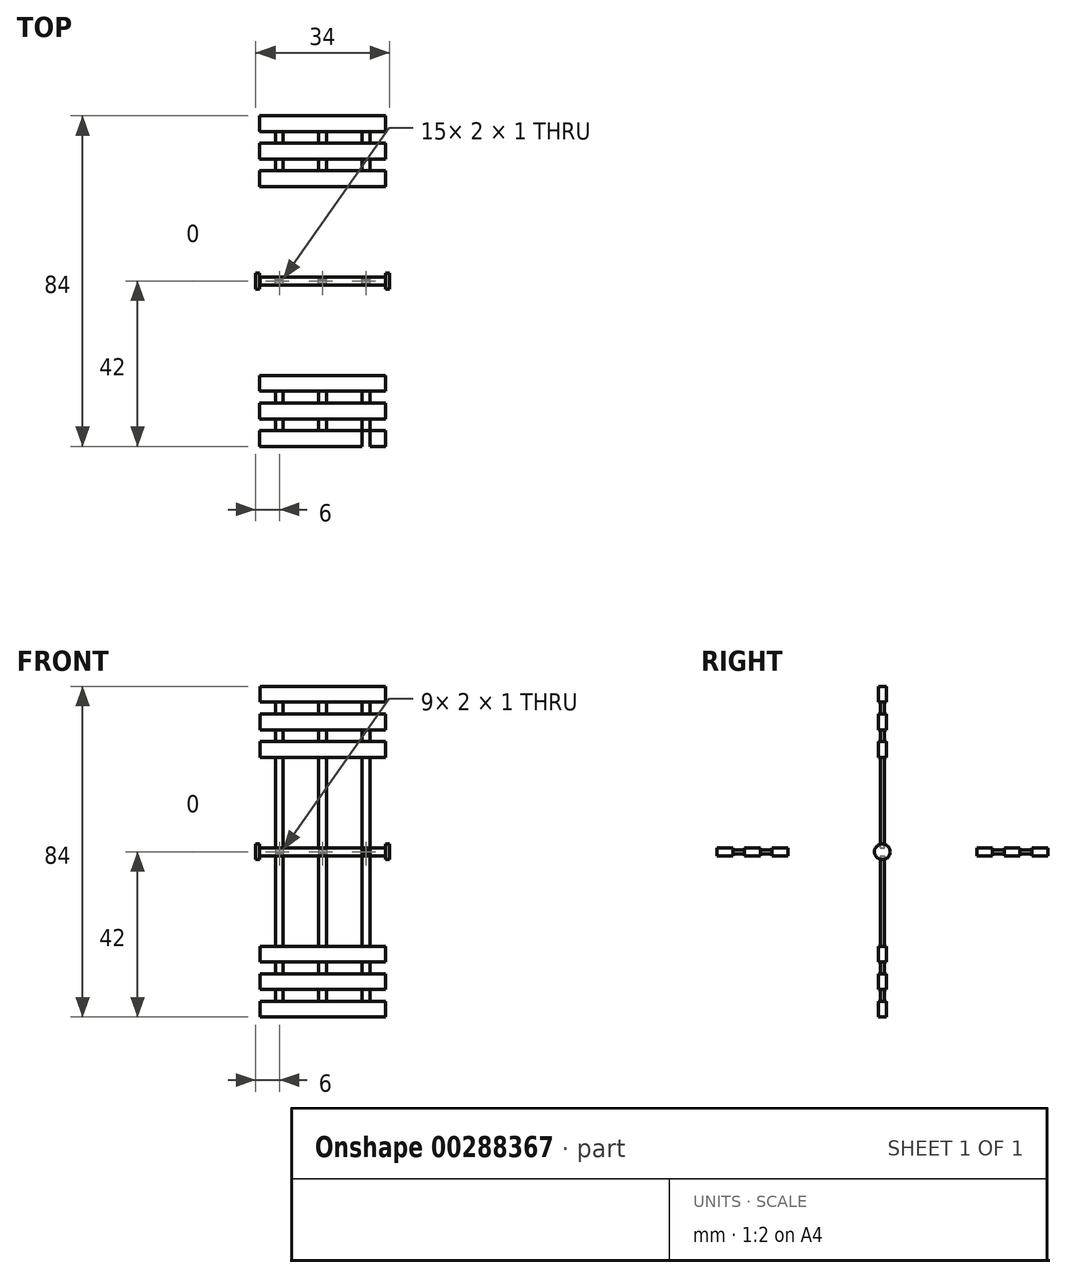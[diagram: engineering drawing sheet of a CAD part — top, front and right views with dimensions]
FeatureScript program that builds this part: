
annotation { "Feature Type Name" : "Feature", "Feature Type Description" : "" }
export const myFeature = defineFeature(function(context is Context, id is Id, definition is map)
    precondition{}
    {
        {
            var Q0;
            Q0=qCreatedBy(makeId("Top.planeOp"),FACE);
            var sketch = newSketch(context, id + "F0", { "sketchPlane" : qUnion([Q0])});
            skLineSegment(sketch, "E0.bottom", {"start": v(16, 1) * mm, "end": v(-16, 1) * mm});
            skLineSegment(sketch, "E0.top", {"start": v(16, -1) * mm, "end": v(-16, -1) * mm});
            skLineSegment(sketch, "E0.left", {"start": v(16, 1) * mm, "end": v(16, -1) * mm});
            skLineSegment(sketch, "E0.right", {"start": v(-16, 1) * mm, "end": v(-16, -1) * mm});
            skPoint(sketch, "E0.middle", {"position": v(0, 0) * mm});
            skLineSegment(sketch, "E1.bottom", {"start": v(16, 2) * mm, "end": v(17, 2) * mm});
            skLineSegment(sketch, "E1.right", {"start": v(17, 2) * mm, "end": v(17, -2) * mm});
            skPoint(sketch, "E1.middle", {"position": v(16.5, 0) * mm});
            skLineSegment(sketch, "E2.MirrorCS", {"start": v(-16, 1) * mm, "end": v(16, 1) * mm});
            skLineSegment(sketch, "E3.MirrorCS", {"start": v(-16, -1) * mm, "end": v(16, -1) * mm});
            skLineSegment(sketch, "E4.MirrorCS", {"start": v(-17, 2) * mm, "end": v(-17, -2) * mm});
            skLineSegment(sketch, "E5.MirrorCS", {"start": v(-16, 2) * mm, "end": v(-17, 2) * mm});
            skPoint(sketch, "E6.MirrorP", {"position": v(-16.5, 0) * mm});
            skLineSegment(sketch, "E7.MirrorCS", {"start": v(-16, -2) * mm, "end": v(-17, -2) * mm});
            skLineSegment(sketch, "E8.bottom", {"start": v(1, 1) * mm, "end": v(-1, 1) * mm});
            skLineSegment(sketch, "E8.top", {"start": v(1, 42) * mm, "end": v(-1, 42) * mm});
            skLineSegment(sketch, "E8.left", {"start": v(1, 1) * mm, "end": v(1, 42) * mm});
            skLineSegment(sketch, "E8.right", {"start": v(-1, 1) * mm, "end": v(-1, 42) * mm});
            skPoint(sketch, "E8.middle", {"position": v(0, 21.5) * mm});
            skPoint(sketch, "E8.middle.positionSnap0", {"position": v(0, 1) * mm});
            skPoint(sketch, "E8.centerSnap0", {"position": v(0, 1) * mm});
            skLineSegment(sketch, "E9", {"start": v(1, 6.73) * mm, "end": v(11, 6.73) * mm, "construction": true});
            skLineSegment(sketch, "E10.bottom", {"start": v(12, 1) * mm, "end": v(10, 1) * mm});
            skLineSegment(sketch, "E10.top", {"start": v(12, 42) * mm, "end": v(10, 42) * mm});
            skLineSegment(sketch, "E10.left", {"start": v(12, 1) * mm, "end": v(12, 42) * mm});
            skLineSegment(sketch, "E10.right", {"start": v(10, 1) * mm, "end": v(10, 42) * mm});
            skPoint(sketch, "E10.middle", {"position": v(11, 21.5) * mm});
            skPoint(sketch, "E10.middle.positionSnap0", {"position": v(1, 21.5) * mm});
            skPoint(sketch, "E10.centerSnap0", {"position": v(1, 21.5) * mm});
            skLineSegment(sketch, "E11.MirrorCS", {"start": v(-12, 42) * mm, "end": v(-10, 42) * mm});
            skPoint(sketch, "E12.MirrorP", {"position": v(-11, 21.5) * mm});
            skLineSegment(sketch, "E13.MirrorCS", {"start": v(-12, 1) * mm, "end": v(-10, 1) * mm});
            skLineSegment(sketch, "E14.MirrorCS", {"start": v(-12, 1) * mm, "end": v(-12, 42) * mm});
            skLineSegment(sketch, "E15.MirrorCS", {"start": v(-10, 1) * mm, "end": v(-10, 42) * mm});
            skLineSegment(sketch, "E16", {"start": v(5.79, 42) * mm, "end": v(5.79, 40) * mm, "construction": true});
            skLineSegment(sketch, "E17.bottom", {"start": v(-16, 42) * mm, "end": v(16, 42) * mm});
            skLineSegment(sketch, "E17.top", {"start": v(-16, 38) * mm, "end": v(16, 38) * mm});
            skLineSegment(sketch, "E17.left", {"start": v(-16, 42) * mm, "end": v(-16, 38) * mm});
            skLineSegment(sketch, "E17.right", {"start": v(16, 42) * mm, "end": v(16, 38) * mm});
            skPoint(sketch, "E17.middle", {"position": v(0, 40) * mm});
            skLineSegment(sketch, "E18", {"start": v(16, 38) * mm, "end": v(16, 35) * mm, "construction": true});
            skLineSegment(sketch, "E19.bottom", {"start": v(16, 35) * mm, "end": v(-16, 35) * mm});
            skLineSegment(sketch, "E19.top", {"start": v(16, 31) * mm, "end": v(-16, 31) * mm});
            skLineSegment(sketch, "E19.left", {"start": v(16, 35) * mm, "end": v(16, 31) * mm});
            skLineSegment(sketch, "E19.right", {"start": v(-16, 35) * mm, "end": v(-16, 31) * mm});
            skLineSegment(sketch, "E20", {"start": v(16, 31) * mm, "end": v(16, 28) * mm, "construction": true});
            skLineSegment(sketch, "E21.bottom", {"start": v(16, 28) * mm, "end": v(-16, 28) * mm});
            skLineSegment(sketch, "E21.top", {"start": v(16, 24) * mm, "end": v(-16, 24) * mm});
            skLineSegment(sketch, "E21.left", {"start": v(16, 28) * mm, "end": v(16, 24) * mm});
            skLineSegment(sketch, "E21.right", {"start": v(-16, 28) * mm, "end": v(-16, 24) * mm});
            skLineSegment(sketch, "E22.MirrorCS", {"start": v(16, -2) * mm, "end": v(17, -2) * mm});
            skLineSegment(sketch, "E23.MirrorCS", {"start": v(12, -42) * mm, "end": v(10, -42) * mm});
            skLineSegment(sketch, "E24.MirrorCS", {"start": v(-16, -2) * mm, "end": v(-16, 2) * mm});
            skLineSegment(sketch, "E25.MirrorCS", {"start": v(16, -2) * mm, "end": v(16, 2) * mm});
            skPoint(sketch, "E26.MirrorP", {"position": v(0, -1) * mm});
            skLineSegment(sketch, "E27.MirrorCS", {"start": v(5.79, -42) * mm, "end": v(5.79, -40) * mm, "construction": true});
            skPoint(sketch, "E28.MirrorP", {"position": v(1, -21.5) * mm});
            skLineSegment(sketch, "E29.MirrorCS", {"start": v(16, -35) * mm, "end": v(-16, -35) * mm});
            skPoint(sketch, "E30.MirrorP", {"position": v(0, -21.5) * mm});
            skLineSegment(sketch, "E31.MirrorCS", {"start": v(-1, -1) * mm, "end": v(-1, -42) * mm});
            skLineSegment(sketch, "E32.MirrorCS", {"start": v(16, -28) * mm, "end": v(16, -24) * mm});
            skLineSegment(sketch, "E33.MirrorCS", {"start": v(16, -38) * mm, "end": v(16, -35) * mm, "construction": true});
            skLineSegment(sketch, "E34.MirrorCS", {"start": v(1, -1) * mm, "end": v(1, -42) * mm});
            skLineSegment(sketch, "E35.MirrorCS", {"start": v(-12, -42) * mm, "end": v(-10, -42) * mm});
            skLineSegment(sketch, "E36.MirrorCS", {"start": v(-16, -28) * mm, "end": v(-16, -24) * mm});
            skLineSegment(sketch, "E37.MirrorCS", {"start": v(-12, -1) * mm, "end": v(-12, -42) * mm});
            skLineSegment(sketch, "E38.MirrorCS", {"start": v(1, -6.73) * mm, "end": v(11, -6.73) * mm, "construction": true});
            skLineSegment(sketch, "E39.MirrorCS", {"start": v(16, -42) * mm, "end": v(16, -38) * mm});
            skLineSegment(sketch, "E40.MirrorCS", {"start": v(16, -24) * mm, "end": v(-16, -24) * mm});
            skLineSegment(sketch, "E41.MirrorCS", {"start": v(16, -31) * mm, "end": v(-16, -31) * mm});
            skLineSegment(sketch, "E42.MirrorCS", {"start": v(1, -42) * mm, "end": v(-1, -42) * mm});
            skPoint(sketch, "E43.MirrorP", {"position": v(0, -40) * mm});
            skLineSegment(sketch, "E44.MirrorCS", {"start": v(-16, -42) * mm, "end": v(16, -42) * mm});
            skLineSegment(sketch, "E45.MirrorCS", {"start": v(16, -35) * mm, "end": v(16, -31) * mm});
            skLineSegment(sketch, "E46.MirrorCS", {"start": v(-10, -1) * mm, "end": v(-10, -42) * mm});
            skPoint(sketch, "E47.MirrorP", {"position": v(11, -21.5) * mm});
            skLineSegment(sketch, "E48.MirrorCS", {"start": v(-16, -35) * mm, "end": v(-16, -31) * mm});
            skLineSegment(sketch, "E49.MirrorCS", {"start": v(-16, -38) * mm, "end": v(16, -38) * mm});
            skLineSegment(sketch, "E50.MirrorCS", {"start": v(12, -1) * mm, "end": v(12, -42) * mm});
            skLineSegment(sketch, "E51.MirrorCS", {"start": v(16, -31) * mm, "end": v(16, -28) * mm, "construction": true});
            skLineSegment(sketch, "E52.MirrorCS", {"start": v(-16, -42) * mm, "end": v(-16, -38) * mm});
            skLineSegment(sketch, "E53.MirrorCS", {"start": v(16, -28) * mm, "end": v(-16, -28) * mm});
            skLineSegment(sketch, "E54.MirrorCS", {"start": v(10, -1) * mm, "end": v(10, -42) * mm});
            skPoint(sketch, "E55.MirrorP", {"position": v(-11, -21.5) * mm});
            skLineSegment(sketch, "E56", {"start": v(-17, 0) * mm, "end": v(17, 0) * mm});
            skSolve(sketch);
        }
        {
            var Q0;
            {var subQ4=sQuery(id+"F0.wireOp",EDGE,"E7.MirrorCS");Q0=makeQuery(id+"F0.imprint","IMPRINT",FACE,{"disambiguationData":[TD([[makeQuery(id+"F0.imprint","IMPRINT",EDGE,{"derivedFrom":subQ4}),-1.0]])]});}
            var Q1;
            {var subQ0=sQuery(id+"F0.wireOp",EDGE,"E3.MirrorCS");var subQ5=sQuery(id+"F0.wireOp",EDGE,"E24.MirrorCS");var subQ6=makeQuery(id+"F0.imprint","INTERSECT",VERTEX,{"derivedFrom":[subQ0,subQ5]});Q1=makeQuery(id+"F0.imprint","IMPRINT",FACE,{"disambiguationData":[TD([[makeQuery(id+"F0.imprint","IMPRINT",EDGE,{"disambiguationData":[TD([[subQ6,-1.0]])],"derivedFrom":subQ0}),1.0]])]});}
            var Q2;
            {var subQ4=sQuery(id+"F0.wireOp",EDGE,"E22.MirrorCS");Q2=makeQuery(id+"F0.imprint","IMPRINT",FACE,{"disambiguationData":[TD([[makeQuery(id+"F0.imprint","IMPRINT",EDGE,{"derivedFrom":subQ4}),1.0]])]});}
            var Q3;
            Q3=sQuery(id+"F0.wireOp",EDGE,"E56");
            revolve(context, id + "F1", {"entities" : qUnion([Q0, Q1, Q2]), "axis" : qUnion([Q3]), "revolveType" : RevolveType.FULL});
        }
        {
            var Q0;
            {var subQ0=sQuery(id+"F0.wireOp",EDGE,"E37.MirrorCS");var subQ1=sQuery(id+"F0.wireOp",EDGE,"E3.MirrorCS");var subQ2=makeQuery(id+"F0.imprint","INTERSECT",VERTEX,{"derivedFrom":[subQ1,subQ0]});Q0=makeQuery(id+"F0.imprint","IMPRINT",FACE,{"disambiguationData":[TD([[makeQuery(id+"F0.imprint","IMPRINT",EDGE,{"disambiguationData":[TD([[subQ2,-1.0]])],"derivedFrom":subQ1}),-1.0]])]});}
            var Q1;
            {var subQ0=sQuery(id+"F0.wireOp",EDGE,"E31.MirrorCS");var subQ1=sQuery(id+"F0.wireOp",EDGE,"E3.MirrorCS");var subQ2=makeQuery(id+"F0.imprint","INTERSECT",VERTEX,{"derivedFrom":[subQ1,subQ0]});Q1=makeQuery(id+"F0.imprint","IMPRINT",FACE,{"disambiguationData":[TD([[makeQuery(id+"F0.imprint","IMPRINT",EDGE,{"disambiguationData":[TD([[subQ2,-1.0]])],"derivedFrom":subQ1}),-1.0]])]});}
            var Q2;
            {var subQ0=sQuery(id+"F0.wireOp",EDGE,"E50.MirrorCS");var subQ1=sQuery(id+"F0.wireOp",EDGE,"E3.MirrorCS");var subQ2=makeQuery(id+"F0.imprint","INTERSECT",VERTEX,{"derivedFrom":[subQ1,subQ0]});Q2=makeQuery(id+"F0.imprint","IMPRINT",FACE,{"disambiguationData":[TD([[makeQuery(id+"F0.imprint","IMPRINT",EDGE,{"disambiguationData":[TD([[subQ2,1.0]])],"derivedFrom":subQ1}),-1.0]])]});}
            var Q3;
            {var subQ0=sQuery(id+"F0.wireOp",EDGE,"E53.MirrorCS");var subQ1=sQuery(id+"F0.wireOp",EDGE,"E31.MirrorCS");var subQ2=makeQuery(id+"F0.imprint","INTERSECT",VERTEX,{"derivedFrom":[subQ1,subQ0]});Q3=makeQuery(id+"F0.imprint","IMPRINT",FACE,{"disambiguationData":[TD([[makeQuery(id+"F0.imprint","IMPRINT",EDGE,{"disambiguationData":[TD([[subQ2,-1.0]])],"derivedFrom":subQ1}),1.0]])]});}
            var Q4;
            {var subQ0=sQuery(id+"F0.wireOp",EDGE,"E53.MirrorCS");var subQ1=sQuery(id+"F0.wireOp",EDGE,"E37.MirrorCS");var subQ2=makeQuery(id+"F0.imprint","INTERSECT",VERTEX,{"derivedFrom":[subQ1,subQ0]});Q4=makeQuery(id+"F0.imprint","IMPRINT",FACE,{"disambiguationData":[TD([[makeQuery(id+"F0.imprint","IMPRINT",EDGE,{"disambiguationData":[TD([[subQ2,-1.0]])],"derivedFrom":subQ1}),1.0]])]});}
            var Q5;
            {var subQ0=sQuery(id+"F0.wireOp",EDGE,"E37.MirrorCS");var subQ1=sQuery(id+"F0.wireOp",EDGE,"E29.MirrorCS");var subQ2=makeQuery(id+"F0.imprint","INTERSECT",VERTEX,{"derivedFrom":[subQ1,subQ0]});Q5=makeQuery(id+"F0.imprint","IMPRINT",FACE,{"disambiguationData":[TD([[makeQuery(id+"F0.imprint","IMPRINT",EDGE,{"disambiguationData":[TD([[subQ2,1.0]])],"derivedFrom":subQ1}),1.0]])]});}
            var Q6;
            {var subQ0=sQuery(id+"F0.wireOp",EDGE,"E34.MirrorCS");var subQ1=sQuery(id+"F0.wireOp",EDGE,"E29.MirrorCS");var subQ2=makeQuery(id+"F0.imprint","INTERSECT",VERTEX,{"derivedFrom":[subQ1,subQ0]});Q6=makeQuery(id+"F0.imprint","IMPRINT",FACE,{"disambiguationData":[TD([[makeQuery(id+"F0.imprint","IMPRINT",EDGE,{"disambiguationData":[TD([[subQ2,-1.0]])],"derivedFrom":subQ1}),1.0]])]});}
            var Q7;
            {var subQ0=sQuery(id+"F0.wireOp",EDGE,"E50.MirrorCS");var subQ1=sQuery(id+"F0.wireOp",EDGE,"E41.MirrorCS");var subQ2=makeQuery(id+"F0.imprint","INTERSECT",VERTEX,{"derivedFrom":[subQ1,subQ0]});Q7=makeQuery(id+"F0.imprint","IMPRINT",FACE,{"disambiguationData":[TD([[makeQuery(id+"F0.imprint","IMPRINT",EDGE,{"disambiguationData":[TD([[subQ2,-1.0]])],"derivedFrom":subQ1}),-1.0]])]});}
            var Q8;
            {var subQ0=sQuery(id+"F0.wireOp",EDGE,"E50.MirrorCS");var subQ1=sQuery(id+"F0.wireOp",EDGE,"E29.MirrorCS");var subQ2=makeQuery(id+"F0.imprint","INTERSECT",VERTEX,{"derivedFrom":[subQ1,subQ0]});Q8=makeQuery(id+"F0.imprint","IMPRINT",FACE,{"disambiguationData":[TD([[makeQuery(id+"F0.imprint","IMPRINT",EDGE,{"disambiguationData":[TD([[subQ2,-1.0]])],"derivedFrom":subQ1}),1.0]])]});}
            var Q9;
            {var subQ0=sQuery(id+"F0.wireOp",EDGE,"E8.bottom");Q9=makeQuery(id+"F0.imprint","IMPRINT",FACE,{"disambiguationData":[TD([[makeQuery(id+"F0.imprint","IMPRINT",EDGE,{"derivedFrom":subQ0}),-1.0]])]});}
            var Q10;
            {var subQ0=sQuery(id+"F0.wireOp",EDGE,"E13.MirrorCS");Q10=makeQuery(id+"F0.imprint","IMPRINT",FACE,{"disambiguationData":[TD([[makeQuery(id+"F0.imprint","IMPRINT",EDGE,{"derivedFrom":subQ0}),1.0]])]});}
            var Q11;
            {var subQ0=sQuery(id+"F0.wireOp",EDGE,"E10.bottom");Q11=makeQuery(id+"F0.imprint","IMPRINT",FACE,{"disambiguationData":[TD([[makeQuery(id+"F0.imprint","IMPRINT",EDGE,{"derivedFrom":subQ0}),-1.0]])]});}
            var Q12;
            {var subQ0=sQuery(id+"F0.wireOp",EDGE,"E21.bottom");var subQ1=sQuery(id+"F0.wireOp",EDGE,"E14.MirrorCS");var subQ2=makeQuery(id+"F0.imprint","INTERSECT",VERTEX,{"derivedFrom":[subQ1,subQ0]});Q12=makeQuery(id+"F0.imprint","IMPRINT",FACE,{"disambiguationData":[TD([[makeQuery(id+"F0.imprint","IMPRINT",EDGE,{"disambiguationData":[TD([[subQ2,-1.0]])],"derivedFrom":subQ1}),-1.0]])]});}
            var Q13;
            {var subQ0=sQuery(id+"F0.wireOp",EDGE,"E21.bottom");var subQ1=sQuery(id+"F0.wireOp",EDGE,"E8.left");var subQ2=makeQuery(id+"F0.imprint","INTERSECT",VERTEX,{"derivedFrom":[subQ1,subQ0]});Q13=makeQuery(id+"F0.imprint","IMPRINT",FACE,{"disambiguationData":[TD([[makeQuery(id+"F0.imprint","IMPRINT",EDGE,{"disambiguationData":[TD([[subQ2,-1.0]])],"derivedFrom":subQ1}),1.0]])]});}
            var Q14;
            {var subQ0=sQuery(id+"F0.wireOp",EDGE,"E21.bottom");var subQ1=sQuery(id+"F0.wireOp",EDGE,"E10.left");var subQ2=makeQuery(id+"F0.imprint","INTERSECT",VERTEX,{"derivedFrom":[subQ1,subQ0]});Q14=makeQuery(id+"F0.imprint","IMPRINT",FACE,{"disambiguationData":[TD([[makeQuery(id+"F0.imprint","IMPRINT",EDGE,{"disambiguationData":[TD([[subQ2,-1.0]])],"derivedFrom":subQ1}),1.0]])]});}
            var Q15;
            {var subQ0=sQuery(id+"F0.wireOp",EDGE,"E19.bottom");var subQ1=sQuery(id+"F0.wireOp",EDGE,"E10.left");var subQ2=makeQuery(id+"F0.imprint","INTERSECT",VERTEX,{"derivedFrom":[subQ1,subQ0]});Q15=makeQuery(id+"F0.imprint","IMPRINT",FACE,{"disambiguationData":[TD([[makeQuery(id+"F0.imprint","IMPRINT",EDGE,{"disambiguationData":[TD([[subQ2,-1.0]])],"derivedFrom":subQ1}),1.0]])]});}
            var Q16;
            {var subQ0=sQuery(id+"F0.wireOp",EDGE,"E19.bottom");var subQ1=sQuery(id+"F0.wireOp",EDGE,"E8.left");var subQ2=makeQuery(id+"F0.imprint","INTERSECT",VERTEX,{"derivedFrom":[subQ1,subQ0]});Q16=makeQuery(id+"F0.imprint","IMPRINT",FACE,{"disambiguationData":[TD([[makeQuery(id+"F0.imprint","IMPRINT",EDGE,{"disambiguationData":[TD([[subQ2,-1.0]])],"derivedFrom":subQ1}),1.0]])]});}
            var Q17;
            {var subQ0=sQuery(id+"F0.wireOp",EDGE,"E19.bottom");var subQ1=sQuery(id+"F0.wireOp",EDGE,"E14.MirrorCS");var subQ2=makeQuery(id+"F0.imprint","INTERSECT",VERTEX,{"derivedFrom":[subQ1,subQ0]});Q17=makeQuery(id+"F0.imprint","IMPRINT",FACE,{"disambiguationData":[TD([[makeQuery(id+"F0.imprint","IMPRINT",EDGE,{"disambiguationData":[TD([[subQ2,-1.0]])],"derivedFrom":subQ1}),-1.0]])]});}
            extrude(context, id + "F2", {"entities" : qUnion([Q0, Q1, Q2, Q3, Q4, Q5, Q6, Q7, Q8, Q9, Q10, Q11, Q12, Q13, Q14, Q15, Q16, Q17]), "operationType" : NewBodyOperationType.ADD, "endBound" : BoundingType.SYMMETRIC, "depth" : 1 * mm});
        }
        {
            var Q0;
            {var subQ0=sQuery(id+"F0.wireOp",EDGE,"E44.MirrorCS");var subQ1=sQuery(id+"F0.wireOp",EDGE,"E31.MirrorCS");var subQ2=makeQuery(id+"F0.imprint","INTERSECT",VERTEX,{"derivedFrom":[subQ1,subQ0]});Q0=makeQuery(id+"F0.imprint","IMPRINT",FACE,{"disambiguationData":[TD([[makeQuery(id+"F0.imprint","IMPRINT",EDGE,{"disambiguationData":[TD([[subQ2,1.0]])],"derivedFrom":subQ1}),-1.0]])]});}
            var Q1;
            {var subQ0=sQuery(id+"F0.wireOp",EDGE,"E44.MirrorCS");var subQ1=sQuery(id+"F0.wireOp",EDGE,"E34.MirrorCS");var subQ2=makeQuery(id+"F0.imprint","INTERSECT",VERTEX,{"derivedFrom":[subQ1,subQ0]});Q1=makeQuery(id+"F0.imprint","IMPRINT",FACE,{"disambiguationData":[TD([[makeQuery(id+"F0.imprint","IMPRINT",EDGE,{"disambiguationData":[TD([[subQ2,1.0]])],"derivedFrom":subQ1}),1.0]])]});}
            var Q2;
            {var subQ0=sQuery(id+"F0.wireOp",EDGE,"E44.MirrorCS");var subQ1=sQuery(id+"F0.wireOp",EDGE,"E37.MirrorCS");var subQ2=makeQuery(id+"F0.imprint","INTERSECT",VERTEX,{"derivedFrom":[subQ1,subQ0]});Q2=makeQuery(id+"F0.imprint","IMPRINT",FACE,{"disambiguationData":[TD([[makeQuery(id+"F0.imprint","IMPRINT",EDGE,{"disambiguationData":[TD([[subQ2,1.0]])],"derivedFrom":subQ1}),1.0]])]});}
            var Q3;
            {var subQ0=sQuery(id+"F0.wireOp",EDGE,"E50.MirrorCS");var subQ1=sQuery(id+"F0.wireOp",EDGE,"E44.MirrorCS");var subQ2=makeQuery(id+"F0.imprint","INTERSECT",VERTEX,{"derivedFrom":[subQ1,subQ0]});Q3=makeQuery(id+"F0.imprint","IMPRINT",FACE,{"disambiguationData":[TD([[makeQuery(id+"F0.imprint","IMPRINT",EDGE,{"disambiguationData":[TD([[subQ2,1.0]])],"derivedFrom":subQ1}),1.0]])]});}
            var Q4;
            {var subQ5=sQuery(id+"F0.wireOp",EDGE,"E52.MirrorCS");Q4=makeQuery(id+"F0.imprint","IMPRINT",FACE,{"disambiguationData":[TD([[makeQuery(id+"F0.imprint","IMPRINT",EDGE,{"derivedFrom":subQ5}),-1.0]])]});}
            var Q5;
            {var subQ0=sQuery(id+"F0.wireOp",EDGE,"E39.MirrorCS");Q5=makeQuery(id+"F0.imprint","IMPRINT",FACE,{"disambiguationData":[TD([[makeQuery(id+"F0.imprint","IMPRINT",EDGE,{"derivedFrom":subQ0}),1.0]])]});}
            var Q6;
            {var subQ0=sQuery(id+"F0.wireOp",EDGE,"E44.MirrorCS");var subQ1=sQuery(id+"F0.wireOp",EDGE,"E31.MirrorCS");var subQ2=makeQuery(id+"F0.imprint","INTERSECT",VERTEX,{"derivedFrom":[subQ1,subQ0]});Q6=makeQuery(id+"F0.imprint","IMPRINT",FACE,{"disambiguationData":[TD([[makeQuery(id+"F0.imprint","IMPRINT",EDGE,{"disambiguationData":[TD([[subQ2,1.0]])],"derivedFrom":subQ1}),1.0]])]});}
            var Q7;
            {var subQ0=sQuery(id+"F0.wireOp",EDGE,"E45.MirrorCS");Q7=makeQuery(id+"F0.imprint","IMPRINT",FACE,{"disambiguationData":[TD([[makeQuery(id+"F0.imprint","IMPRINT",EDGE,{"derivedFrom":subQ0}),1.0]])]});}
            var Q8;
            {var subQ0=sQuery(id+"F0.wireOp",EDGE,"E50.MirrorCS");var subQ1=sQuery(id+"F0.wireOp",EDGE,"E29.MirrorCS");var subQ2=makeQuery(id+"F0.imprint","INTERSECT",VERTEX,{"derivedFrom":[subQ1,subQ0]});Q8=makeQuery(id+"F0.imprint","IMPRINT",FACE,{"disambiguationData":[TD([[makeQuery(id+"F0.imprint","IMPRINT",EDGE,{"disambiguationData":[TD([[subQ2,-1.0]])],"derivedFrom":subQ1}),-1.0]])]});}
            var Q9;
            {var subQ0=sQuery(id+"F0.wireOp",EDGE,"E54.MirrorCS");var subQ1=sQuery(id+"F0.wireOp",EDGE,"E29.MirrorCS");var subQ2=makeQuery(id+"F0.imprint","INTERSECT",VERTEX,{"derivedFrom":[subQ1,subQ0]});Q9=makeQuery(id+"F0.imprint","IMPRINT",FACE,{"disambiguationData":[TD([[makeQuery(id+"F0.imprint","IMPRINT",EDGE,{"disambiguationData":[TD([[subQ2,-1.0]])],"derivedFrom":subQ1}),-1.0]])]});}
            var Q10;
            {var subQ0=sQuery(id+"F0.wireOp",EDGE,"E34.MirrorCS");var subQ1=sQuery(id+"F0.wireOp",EDGE,"E29.MirrorCS");var subQ2=makeQuery(id+"F0.imprint","INTERSECT",VERTEX,{"derivedFrom":[subQ1,subQ0]});Q10=makeQuery(id+"F0.imprint","IMPRINT",FACE,{"disambiguationData":[TD([[makeQuery(id+"F0.imprint","IMPRINT",EDGE,{"disambiguationData":[TD([[subQ2,-1.0]])],"derivedFrom":subQ1}),-1.0]])]});}
            var Q11;
            {var subQ0=sQuery(id+"F0.wireOp",EDGE,"E31.MirrorCS");var subQ1=sQuery(id+"F0.wireOp",EDGE,"E29.MirrorCS");var subQ2=makeQuery(id+"F0.imprint","INTERSECT",VERTEX,{"derivedFrom":[subQ1,subQ0]});Q11=makeQuery(id+"F0.imprint","IMPRINT",FACE,{"disambiguationData":[TD([[makeQuery(id+"F0.imprint","IMPRINT",EDGE,{"disambiguationData":[TD([[subQ2,-1.0]])],"derivedFrom":subQ1}),-1.0]])]});}
            var Q12;
            {var subQ0=sQuery(id+"F0.wireOp",EDGE,"E37.MirrorCS");var subQ1=sQuery(id+"F0.wireOp",EDGE,"E29.MirrorCS");var subQ2=makeQuery(id+"F0.imprint","INTERSECT",VERTEX,{"derivedFrom":[subQ1,subQ0]});Q12=makeQuery(id+"F0.imprint","IMPRINT",FACE,{"disambiguationData":[TD([[makeQuery(id+"F0.imprint","IMPRINT",EDGE,{"disambiguationData":[TD([[subQ2,1.0]])],"derivedFrom":subQ1}),-1.0]])]});}
            var Q13;
            {var subQ0=sQuery(id+"F0.wireOp",EDGE,"E48.MirrorCS");Q13=makeQuery(id+"F0.imprint","IMPRINT",FACE,{"disambiguationData":[TD([[makeQuery(id+"F0.imprint","IMPRINT",EDGE,{"derivedFrom":subQ0}),-1.0]])]});}
            var Q14;
            {var subQ0=sQuery(id+"F0.wireOp",EDGE,"E36.MirrorCS");Q14=makeQuery(id+"F0.imprint","IMPRINT",FACE,{"disambiguationData":[TD([[makeQuery(id+"F0.imprint","IMPRINT",EDGE,{"derivedFrom":subQ0}),-1.0]])]});}
            var Q15;
            {var subQ0=sQuery(id+"F0.wireOp",EDGE,"E40.MirrorCS");var subQ1=sQuery(id+"F0.wireOp",EDGE,"E37.MirrorCS");var subQ2=makeQuery(id+"F0.imprint","INTERSECT",VERTEX,{"derivedFrom":[subQ1,subQ0]});Q15=makeQuery(id+"F0.imprint","IMPRINT",FACE,{"disambiguationData":[TD([[makeQuery(id+"F0.imprint","IMPRINT",EDGE,{"disambiguationData":[TD([[subQ2,-1.0]])],"derivedFrom":subQ1}),1.0]])]});}
            var Q16;
            {var subQ0=sQuery(id+"F0.wireOp",EDGE,"E40.MirrorCS");var subQ1=sQuery(id+"F0.wireOp",EDGE,"E31.MirrorCS");var subQ2=makeQuery(id+"F0.imprint","INTERSECT",VERTEX,{"derivedFrom":[subQ1,subQ0]});Q16=makeQuery(id+"F0.imprint","IMPRINT",FACE,{"disambiguationData":[TD([[makeQuery(id+"F0.imprint","IMPRINT",EDGE,{"disambiguationData":[TD([[subQ2,-1.0]])],"derivedFrom":subQ1}),-1.0]])]});}
            var Q17;
            {var subQ0=sQuery(id+"F0.wireOp",EDGE,"E40.MirrorCS");var subQ1=sQuery(id+"F0.wireOp",EDGE,"E31.MirrorCS");var subQ2=makeQuery(id+"F0.imprint","INTERSECT",VERTEX,{"derivedFrom":[subQ1,subQ0]});Q17=makeQuery(id+"F0.imprint","IMPRINT",FACE,{"disambiguationData":[TD([[makeQuery(id+"F0.imprint","IMPRINT",EDGE,{"disambiguationData":[TD([[subQ2,-1.0]])],"derivedFrom":subQ1}),1.0]])]});}
            var Q18;
            {var subQ0=sQuery(id+"F0.wireOp",EDGE,"E40.MirrorCS");var subQ1=sQuery(id+"F0.wireOp",EDGE,"E34.MirrorCS");var subQ2=makeQuery(id+"F0.imprint","INTERSECT",VERTEX,{"derivedFrom":[subQ1,subQ0]});Q18=makeQuery(id+"F0.imprint","IMPRINT",FACE,{"disambiguationData":[TD([[makeQuery(id+"F0.imprint","IMPRINT",EDGE,{"disambiguationData":[TD([[subQ2,-1.0]])],"derivedFrom":subQ1}),1.0]])]});}
            var Q19;
            {var subQ0=sQuery(id+"F0.wireOp",EDGE,"E50.MirrorCS");var subQ1=sQuery(id+"F0.wireOp",EDGE,"E40.MirrorCS");var subQ2=makeQuery(id+"F0.imprint","INTERSECT",VERTEX,{"derivedFrom":[subQ1,subQ0]});Q19=makeQuery(id+"F0.imprint","IMPRINT",FACE,{"disambiguationData":[TD([[makeQuery(id+"F0.imprint","IMPRINT",EDGE,{"disambiguationData":[TD([[subQ2,-1.0]])],"derivedFrom":subQ1}),1.0]])]});}
            var Q20;
            {var subQ0=sQuery(id+"F0.wireOp",EDGE,"E32.MirrorCS");Q20=makeQuery(id+"F0.imprint","IMPRINT",FACE,{"disambiguationData":[TD([[makeQuery(id+"F0.imprint","IMPRINT",EDGE,{"derivedFrom":subQ0}),1.0]])]});}
            var Q21;
            {var subQ5=sQuery(id+"F0.wireOp",EDGE,"E21.left");Q21=makeQuery(id+"F0.imprint","IMPRINT",FACE,{"disambiguationData":[TD([[makeQuery(id+"F0.imprint","IMPRINT",EDGE,{"derivedFrom":subQ5}),-1.0]])]});}
            var Q22;
            {var subQ0=sQuery(id+"F0.wireOp",EDGE,"E21.top");var subQ1=sQuery(id+"F0.wireOp",EDGE,"E10.left");var subQ2=makeQuery(id+"F0.imprint","INTERSECT",VERTEX,{"derivedFrom":[subQ1,subQ0]});Q22=makeQuery(id+"F0.imprint","IMPRINT",FACE,{"disambiguationData":[TD([[makeQuery(id+"F0.imprint","IMPRINT",EDGE,{"disambiguationData":[TD([[subQ2,-1.0]])],"derivedFrom":subQ1}),1.0]])]});}
            var Q23;
            {var subQ0=sQuery(id+"F0.wireOp",EDGE,"E21.top");var subQ1=sQuery(id+"F0.wireOp",EDGE,"E8.left");var subQ2=makeQuery(id+"F0.imprint","INTERSECT",VERTEX,{"derivedFrom":[subQ1,subQ0]});Q23=makeQuery(id+"F0.imprint","IMPRINT",FACE,{"disambiguationData":[TD([[makeQuery(id+"F0.imprint","IMPRINT",EDGE,{"disambiguationData":[TD([[subQ2,-1.0]])],"derivedFrom":subQ1}),-1.0]])]});}
            var Q24;
            {var subQ0=sQuery(id+"F0.wireOp",EDGE,"E21.top");var subQ1=sQuery(id+"F0.wireOp",EDGE,"E8.left");var subQ2=makeQuery(id+"F0.imprint","INTERSECT",VERTEX,{"derivedFrom":[subQ1,subQ0]});Q24=makeQuery(id+"F0.imprint","IMPRINT",FACE,{"disambiguationData":[TD([[makeQuery(id+"F0.imprint","IMPRINT",EDGE,{"disambiguationData":[TD([[subQ2,-1.0]])],"derivedFrom":subQ1}),1.0]])]});}
            var Q25;
            {var subQ0=sQuery(id+"F0.wireOp",EDGE,"E21.top");var subQ1=sQuery(id+"F0.wireOp",EDGE,"E8.right");var subQ2=makeQuery(id+"F0.imprint","INTERSECT",VERTEX,{"derivedFrom":[subQ1,subQ0]});Q25=makeQuery(id+"F0.imprint","IMPRINT",FACE,{"disambiguationData":[TD([[makeQuery(id+"F0.imprint","IMPRINT",EDGE,{"disambiguationData":[TD([[subQ2,-1.0]])],"derivedFrom":subQ1}),1.0]])]});}
            var Q26;
            {var subQ0=sQuery(id+"F0.wireOp",EDGE,"E21.top");var subQ1=sQuery(id+"F0.wireOp",EDGE,"E14.MirrorCS");var subQ2=makeQuery(id+"F0.imprint","INTERSECT",VERTEX,{"derivedFrom":[subQ1,subQ0]});Q26=makeQuery(id+"F0.imprint","IMPRINT",FACE,{"disambiguationData":[TD([[makeQuery(id+"F0.imprint","IMPRINT",EDGE,{"disambiguationData":[TD([[subQ2,-1.0]])],"derivedFrom":subQ1}),-1.0]])]});}
            var Q27;
            {var subQ5=sQuery(id+"F0.wireOp",EDGE,"E21.right");Q27=makeQuery(id+"F0.imprint","IMPRINT",FACE,{"disambiguationData":[TD([[makeQuery(id+"F0.imprint","IMPRINT",EDGE,{"derivedFrom":subQ5}),1.0]])]});}
            var Q28;
            {var subQ5=sQuery(id+"F0.wireOp",EDGE,"E19.right");Q28=makeQuery(id+"F0.imprint","IMPRINT",FACE,{"disambiguationData":[TD([[makeQuery(id+"F0.imprint","IMPRINT",EDGE,{"derivedFrom":subQ5}),1.0]])]});}
            var Q29;
            {var subQ0=sQuery(id+"F0.wireOp",EDGE,"E19.top");var subQ1=sQuery(id+"F0.wireOp",EDGE,"E14.MirrorCS");var subQ2=makeQuery(id+"F0.imprint","INTERSECT",VERTEX,{"derivedFrom":[subQ1,subQ0]});Q29=makeQuery(id+"F0.imprint","IMPRINT",FACE,{"disambiguationData":[TD([[makeQuery(id+"F0.imprint","IMPRINT",EDGE,{"disambiguationData":[TD([[subQ2,-1.0]])],"derivedFrom":subQ1}),-1.0]])]});}
            var Q30;
            {var subQ0=sQuery(id+"F0.wireOp",EDGE,"E19.top");var subQ1=sQuery(id+"F0.wireOp",EDGE,"E8.right");var subQ2=makeQuery(id+"F0.imprint","INTERSECT",VERTEX,{"derivedFrom":[subQ1,subQ0]});Q30=makeQuery(id+"F0.imprint","IMPRINT",FACE,{"disambiguationData":[TD([[makeQuery(id+"F0.imprint","IMPRINT",EDGE,{"disambiguationData":[TD([[subQ2,-1.0]])],"derivedFrom":subQ1}),1.0]])]});}
            var Q31;
            {var subQ0=sQuery(id+"F0.wireOp",EDGE,"E19.top");var subQ1=sQuery(id+"F0.wireOp",EDGE,"E8.left");var subQ2=makeQuery(id+"F0.imprint","INTERSECT",VERTEX,{"derivedFrom":[subQ1,subQ0]});Q31=makeQuery(id+"F0.imprint","IMPRINT",FACE,{"disambiguationData":[TD([[makeQuery(id+"F0.imprint","IMPRINT",EDGE,{"disambiguationData":[TD([[subQ2,-1.0]])],"derivedFrom":subQ1}),1.0]])]});}
            var Q32;
            {var subQ0=sQuery(id+"F0.wireOp",EDGE,"E19.top");var subQ1=sQuery(id+"F0.wireOp",EDGE,"E8.left");var subQ2=makeQuery(id+"F0.imprint","INTERSECT",VERTEX,{"derivedFrom":[subQ1,subQ0]});Q32=makeQuery(id+"F0.imprint","IMPRINT",FACE,{"disambiguationData":[TD([[makeQuery(id+"F0.imprint","IMPRINT",EDGE,{"disambiguationData":[TD([[subQ2,-1.0]])],"derivedFrom":subQ1}),-1.0]])]});}
            var Q33;
            {var subQ0=sQuery(id+"F0.wireOp",EDGE,"E19.top");var subQ1=sQuery(id+"F0.wireOp",EDGE,"E10.left");var subQ2=makeQuery(id+"F0.imprint","INTERSECT",VERTEX,{"derivedFrom":[subQ1,subQ0]});Q33=makeQuery(id+"F0.imprint","IMPRINT",FACE,{"disambiguationData":[TD([[makeQuery(id+"F0.imprint","IMPRINT",EDGE,{"disambiguationData":[TD([[subQ2,-1.0]])],"derivedFrom":subQ1}),1.0]])]});}
            var Q34;
            {var subQ5=sQuery(id+"F0.wireOp",EDGE,"E19.left");Q34=makeQuery(id+"F0.imprint","IMPRINT",FACE,{"disambiguationData":[TD([[makeQuery(id+"F0.imprint","IMPRINT",EDGE,{"derivedFrom":subQ5}),-1.0]])]});}
            var Q35;
            {var subQ5=sQuery(id+"F0.wireOp",EDGE,"E17.right");Q35=makeQuery(id+"F0.imprint","IMPRINT",FACE,{"disambiguationData":[TD([[makeQuery(id+"F0.imprint","IMPRINT",EDGE,{"derivedFrom":subQ5}),-1.0]])]});}
            var Q36;
            {var subQ0=sQuery(id+"F0.wireOp",EDGE,"E17.bottom");var subQ1=sQuery(id+"F0.wireOp",EDGE,"E10.left");var subQ2=makeQuery(id+"F0.imprint","INTERSECT",VERTEX,{"derivedFrom":[subQ1,subQ0]});Q36=makeQuery(id+"F0.imprint","IMPRINT",FACE,{"disambiguationData":[TD([[makeQuery(id+"F0.imprint","IMPRINT",EDGE,{"disambiguationData":[TD([[subQ2,1.0]])],"derivedFrom":subQ1}),1.0]])]});}
            var Q37;
            {var subQ0=sQuery(id+"F0.wireOp",EDGE,"E17.bottom");var subQ1=sQuery(id+"F0.wireOp",EDGE,"E8.left");var subQ2=makeQuery(id+"F0.imprint","INTERSECT",VERTEX,{"derivedFrom":[subQ1,subQ0]});Q37=makeQuery(id+"F0.imprint","IMPRINT",FACE,{"disambiguationData":[TD([[makeQuery(id+"F0.imprint","IMPRINT",EDGE,{"disambiguationData":[TD([[subQ2,1.0]])],"derivedFrom":subQ1}),-1.0]])]});}
            var Q38;
            {var subQ0=sQuery(id+"F0.wireOp",EDGE,"E17.bottom");var subQ1=sQuery(id+"F0.wireOp",EDGE,"E8.left");var subQ2=makeQuery(id+"F0.imprint","INTERSECT",VERTEX,{"derivedFrom":[subQ1,subQ0]});Q38=makeQuery(id+"F0.imprint","IMPRINT",FACE,{"disambiguationData":[TD([[makeQuery(id+"F0.imprint","IMPRINT",EDGE,{"disambiguationData":[TD([[subQ2,1.0]])],"derivedFrom":subQ1}),1.0]])]});}
            var Q39;
            {var subQ0=sQuery(id+"F0.wireOp",EDGE,"E17.bottom");var subQ1=sQuery(id+"F0.wireOp",EDGE,"E8.right");var subQ2=makeQuery(id+"F0.imprint","INTERSECT",VERTEX,{"derivedFrom":[subQ1,subQ0]});Q39=makeQuery(id+"F0.imprint","IMPRINT",FACE,{"disambiguationData":[TD([[makeQuery(id+"F0.imprint","IMPRINT",EDGE,{"disambiguationData":[TD([[subQ2,1.0]])],"derivedFrom":subQ1}),1.0]])]});}
            var Q40;
            {var subQ0=sQuery(id+"F0.wireOp",EDGE,"E17.bottom");var subQ1=sQuery(id+"F0.wireOp",EDGE,"E14.MirrorCS");var subQ2=makeQuery(id+"F0.imprint","INTERSECT",VERTEX,{"derivedFrom":[subQ1,subQ0]});Q40=makeQuery(id+"F0.imprint","IMPRINT",FACE,{"disambiguationData":[TD([[makeQuery(id+"F0.imprint","IMPRINT",EDGE,{"disambiguationData":[TD([[subQ2,1.0]])],"derivedFrom":subQ1}),-1.0]])]});}
            var Q41;
            {var subQ5=sQuery(id+"F0.wireOp",EDGE,"E17.left");Q41=makeQuery(id+"F0.imprint","IMPRINT",FACE,{"disambiguationData":[TD([[makeQuery(id+"F0.imprint","IMPRINT",EDGE,{"derivedFrom":subQ5}),1.0]])]});}
            extrude(context, id + "F3", {"entities" : qUnion([Q0, Q1, Q2, Q3, Q4, Q5, Q6, Q7, Q8, Q9, Q10, Q11, Q12, Q13, Q14, Q15, Q16, Q17, Q18, Q19, Q20, Q21, Q22, Q23, Q24, Q25, Q26, Q27, Q28, Q29, Q30, Q31, Q32, Q33, Q34, Q35, Q36, Q37, Q38, Q39, Q40, Q41]), "endBound" : BoundingType.SYMMETRIC, "depth" : 2 * mm});
        }
        {
            var Q0;
            Q0=qCreatedBy(makeId("Front.planeOp"),FACE);
            var sketch = newSketch(context, id + "F4", { "sketchPlane" : qUnion([Q0])});
            skLineSegment(sketch, "E57", {"start": v(3.55, 0) * mm, "end": v(3.55, 1) * mm, "construction": true});
            skLineSegment(sketch, "E58.bottom", {"start": v(1, 1) * mm, "end": v(-1, 1) * mm});
            skLineSegment(sketch, "E58.top", {"start": v(1, 42) * mm, "end": v(-1, 42) * mm});
            skLineSegment(sketch, "E58.left", {"start": v(1, 1) * mm, "end": v(1, 42) * mm});
            skLineSegment(sketch, "E58.right", {"start": v(-1, 1) * mm, "end": v(-1, 42) * mm});
            skPoint(sketch, "E58.middle", {"position": v(0, 21.5) * mm});
            skLineSegment(sketch, "E59", {"start": v(1, 7.07) * mm, "end": v(11, 7.07) * mm, "construction": true});
            skLineSegment(sketch, "E60.bottom", {"start": v(10, 1) * mm, "end": v(12, 1) * mm});
            skLineSegment(sketch, "E60.top", {"start": v(10, 42) * mm, "end": v(12, 42) * mm});
            skLineSegment(sketch, "E60.left", {"start": v(10, 1) * mm, "end": v(10, 42) * mm});
            skLineSegment(sketch, "E60.right", {"start": v(12, 1) * mm, "end": v(12, 42) * mm});
            skPoint(sketch, "E60.middle", {"position": v(11, 21.5) * mm});
            skLineSegment(sketch, "E61", {"start": v(0, 0) * mm, "end": v(0, 4.7) * mm, "construction": true});
            skLineSegment(sketch, "E62.MirrorCS", {"start": v(-10, 1) * mm, "end": v(-10, 42) * mm});
            skLineSegment(sketch, "E63.MirrorCS", {"start": v(-12, 1) * mm, "end": v(-12, 42) * mm});
            skLineSegment(sketch, "E64.MirrorCS", {"start": v(-10, 42) * mm, "end": v(-12, 42) * mm});
            skLineSegment(sketch, "E65", {"start": v(-15.95, 1.1) * mm, "end": v(-15.95, 11.1) * mm, "construction": true});
            skLineSegment(sketch, "E66.bottom", {"start": v(-15.95, 42) * mm, "end": v(16.05, 42) * mm});
            skLineSegment(sketch, "E66.top", {"start": v(-15.95, 38) * mm, "end": v(16.05, 38) * mm});
            skLineSegment(sketch, "E66.left", {"start": v(-15.95, 42) * mm, "end": v(-15.95, 38) * mm});
            skLineSegment(sketch, "E66.right", {"start": v(16.05, 42) * mm, "end": v(16.05, 38) * mm});
            skLineSegment(sketch, "E67", {"start": v(14.26, 38) * mm, "end": v(14.26, 35) * mm, "construction": true});
            skLineSegment(sketch, "E68.bottom", {"start": v(-15.95, 35) * mm, "end": v(16.05, 35) * mm});
            skLineSegment(sketch, "E68.top", {"start": v(-15.95, 31) * mm, "end": v(16.05, 31) * mm});
            skLineSegment(sketch, "E68.left", {"start": v(-15.95, 35) * mm, "end": v(-15.95, 31) * mm});
            skLineSegment(sketch, "E68.right", {"start": v(16.05, 35) * mm, "end": v(16.05, 31) * mm});
            skLineSegment(sketch, "E69", {"start": v(14.26, 31) * mm, "end": v(14.26, 28) * mm, "construction": true});
            skLineSegment(sketch, "E70.bottom", {"start": v(-15.95, 28) * mm, "end": v(16.05, 28) * mm});
            skLineSegment(sketch, "E70.top", {"start": v(-15.95, 24) * mm, "end": v(16.05, 24) * mm});
            skLineSegment(sketch, "E70.left", {"start": v(-15.95, 28) * mm, "end": v(-15.95, 24) * mm});
            skLineSegment(sketch, "E70.right", {"start": v(16.05, 28) * mm, "end": v(16.05, 24) * mm});
            skLineSegment(sketch, "E71", {"start": v(-10, 1) * mm, "end": v(-12, 1) * mm});
            skLineSegment(sketch, "E72.MirrorCS", {"start": v(10, -42) * mm, "end": v(12, -42) * mm});
            skLineSegment(sketch, "E73.MirrorCS", {"start": v(-10, -42) * mm, "end": v(-12, -42) * mm});
            skLineSegment(sketch, "E74.MirrorCS", {"start": v(-10, -1) * mm, "end": v(-12, -1) * mm});
            skLineSegment(sketch, "E75.MirrorCS", {"start": v(10, -1) * mm, "end": v(12, -1) * mm});
            skLineSegment(sketch, "E76.MirrorCS", {"start": v(1, -42) * mm, "end": v(-1, -42) * mm});
            skLineSegment(sketch, "E77.MirrorCS", {"start": v(1, -1) * mm, "end": v(-1, -1) * mm});
            skLineSegment(sketch, "E78.MirrorCS", {"start": v(3.55, 0) * mm, "end": v(3.55, -1) * mm, "construction": true});
            skLineSegment(sketch, "E79.MirrorCS", {"start": v(-15.95, -28) * mm, "end": v(16.05, -28) * mm});
            skLineSegment(sketch, "E80.MirrorCS", {"start": v(-15.95, -42) * mm, "end": v(-15.95, -38) * mm});
            skLineSegment(sketch, "E81.MirrorCS", {"start": v(-15.95, -1.1) * mm, "end": v(-15.95, -11.1) * mm, "construction": true});
            skLineSegment(sketch, "E82.MirrorCS", {"start": v(10, -1) * mm, "end": v(10, -42) * mm});
            skLineSegment(sketch, "E83.MirrorCS", {"start": v(12, -1) * mm, "end": v(12, -42) * mm});
            skLineSegment(sketch, "E84.MirrorCS", {"start": v(-15.95, -35) * mm, "end": v(16.05, -35) * mm});
            skLineSegment(sketch, "E85.MirrorCS", {"start": v(16.05, -35) * mm, "end": v(16.05, -31) * mm});
            skLineSegment(sketch, "E86.MirrorCS", {"start": v(1, -1) * mm, "end": v(1, -42) * mm});
            skLineSegment(sketch, "E87.MirrorCS", {"start": v(0, 0) * mm, "end": v(0, -4.7) * mm, "construction": true});
            skLineSegment(sketch, "E88.MirrorCS", {"start": v(16.05, -28) * mm, "end": v(16.05, -24) * mm});
            skLineSegment(sketch, "E89.MirrorCS", {"start": v(-1, -1) * mm, "end": v(-1, -42) * mm});
            skLineSegment(sketch, "E90.MirrorCS", {"start": v(-10, -1) * mm, "end": v(-10, -42) * mm});
            skLineSegment(sketch, "E91.MirrorCS", {"start": v(-12, -1) * mm, "end": v(-12, -42) * mm});
            skLineSegment(sketch, "E92.MirrorCS", {"start": v(-15.95, -42) * mm, "end": v(16.05, -42) * mm});
            skLineSegment(sketch, "E93.MirrorCS", {"start": v(14.26, -31) * mm, "end": v(14.26, -28) * mm, "construction": true});
            skLineSegment(sketch, "E94.MirrorCS", {"start": v(-15.95, -31) * mm, "end": v(16.05, -31) * mm});
            skPoint(sketch, "E95.MirrorP", {"position": v(0, -21.5) * mm});
            skLineSegment(sketch, "E96.MirrorCS", {"start": v(16.05, -42) * mm, "end": v(16.05, -38) * mm});
            skLineSegment(sketch, "E97.MirrorCS", {"start": v(14.26, -38) * mm, "end": v(14.26, -35) * mm, "construction": true});
            skPoint(sketch, "E98.MirrorP", {"position": v(11, -21.5) * mm});
            skLineSegment(sketch, "E99.MirrorCS", {"start": v(1, -7.07) * mm, "end": v(11, -7.07) * mm, "construction": true});
            skLineSegment(sketch, "E100.MirrorCS", {"start": v(-15.95, -28) * mm, "end": v(-15.95, -24) * mm});
            skLineSegment(sketch, "E101.MirrorCS", {"start": v(-15.95, -35) * mm, "end": v(-15.95, -31) * mm});
            skLineSegment(sketch, "E102.MirrorCS", {"start": v(-15.95, -24) * mm, "end": v(16.05, -24) * mm});
            skLineSegment(sketch, "E103.MirrorCS", {"start": v(-15.95, -38) * mm, "end": v(16.05, -38) * mm});
            skSolve(sketch);
        }
        {
            var Q0;
            {var subQ0=sQuery(id+"F4.wireOp",EDGE,"E58.bottom");Q0=makeQuery(id+"F4.imprint","IMPRINT",FACE,{"disambiguationData":[TD([[makeQuery(id+"F4.imprint","IMPRINT",EDGE,{"derivedFrom":subQ0}),-1.0]])]});}
            var Q1;
            {var subQ0=sQuery(id+"F4.wireOp",EDGE,"E60.bottom");Q1=makeQuery(id+"F4.imprint","IMPRINT",FACE,{"disambiguationData":[TD([[makeQuery(id+"F4.imprint","IMPRINT",EDGE,{"derivedFrom":subQ0}),1.0]])]});}
            var Q2;
            {var subQ0=sQuery(id+"F4.wireOp",EDGE,"E71");Q2=makeQuery(id+"F4.imprint","IMPRINT",FACE,{"disambiguationData":[TD([[makeQuery(id+"F4.imprint","IMPRINT",EDGE,{"derivedFrom":subQ0}),-1.0]])]});}
            var Q3;
            {var subQ0=sQuery(id+"F4.wireOp",EDGE,"E74.MirrorCS");Q3=makeQuery(id+"F4.imprint","IMPRINT",FACE,{"disambiguationData":[TD([[makeQuery(id+"F4.imprint","IMPRINT",EDGE,{"derivedFrom":subQ0}),1.0]])]});}
            var Q4;
            {var subQ0=sQuery(id+"F4.wireOp",EDGE,"E75.MirrorCS");Q4=makeQuery(id+"F4.imprint","IMPRINT",FACE,{"disambiguationData":[TD([[makeQuery(id+"F4.imprint","IMPRINT",EDGE,{"derivedFrom":subQ0}),-1.0]])]});}
            var Q5;
            {var subQ0=sQuery(id+"F4.wireOp",EDGE,"E77.MirrorCS");Q5=makeQuery(id+"F4.imprint","IMPRINT",FACE,{"disambiguationData":[TD([[makeQuery(id+"F4.imprint","IMPRINT",EDGE,{"derivedFrom":subQ0}),1.0]])]});}
            var Q6;
            {var subQ0=sQuery(id+"F4.wireOp",EDGE,"E70.bottom");var subQ1=sQuery(id+"F4.wireOp",EDGE,"E60.left");var subQ2=makeQuery(id+"F4.imprint","INTERSECT",VERTEX,{"derivedFrom":[subQ1,subQ0]});Q6=makeQuery(id+"F4.imprint","IMPRINT",FACE,{"disambiguationData":[TD([[makeQuery(id+"F4.imprint","IMPRINT",EDGE,{"disambiguationData":[TD([[subQ2,-1.0]])],"derivedFrom":subQ1}),-1.0]])]});}
            var Q7;
            {var subQ0=sQuery(id+"F4.wireOp",EDGE,"E68.bottom");var subQ1=sQuery(id+"F4.wireOp",EDGE,"E60.left");var subQ2=makeQuery(id+"F4.imprint","INTERSECT",VERTEX,{"derivedFrom":[subQ1,subQ0]});Q7=makeQuery(id+"F4.imprint","IMPRINT",FACE,{"disambiguationData":[TD([[makeQuery(id+"F4.imprint","IMPRINT",EDGE,{"disambiguationData":[TD([[subQ2,-1.0]])],"derivedFrom":subQ1}),-1.0]])]});}
            var Q8;
            {var subQ0=sQuery(id+"F4.wireOp",EDGE,"E70.bottom");var subQ1=sQuery(id+"F4.wireOp",EDGE,"E62.MirrorCS");var subQ2=makeQuery(id+"F4.imprint","INTERSECT",VERTEX,{"derivedFrom":[subQ1,subQ0]});Q8=makeQuery(id+"F4.imprint","IMPRINT",FACE,{"disambiguationData":[TD([[makeQuery(id+"F4.imprint","IMPRINT",EDGE,{"disambiguationData":[TD([[subQ2,-1.0]])],"derivedFrom":subQ1}),1.0]])]});}
            var Q9;
            {var subQ0=sQuery(id+"F4.wireOp",EDGE,"E68.bottom");var subQ1=sQuery(id+"F4.wireOp",EDGE,"E62.MirrorCS");var subQ2=makeQuery(id+"F4.imprint","INTERSECT",VERTEX,{"derivedFrom":[subQ1,subQ0]});Q9=makeQuery(id+"F4.imprint","IMPRINT",FACE,{"disambiguationData":[TD([[makeQuery(id+"F4.imprint","IMPRINT",EDGE,{"disambiguationData":[TD([[subQ2,-1.0]])],"derivedFrom":subQ1}),1.0]])]});}
            var Q10;
            {var subQ0=sQuery(id+"F4.wireOp",EDGE,"E91.MirrorCS");var subQ1=sQuery(id+"F4.wireOp",EDGE,"E79.MirrorCS");var subQ2=makeQuery(id+"F4.imprint","INTERSECT",VERTEX,{"derivedFrom":[subQ1,subQ0]});Q10=makeQuery(id+"F4.imprint","IMPRINT",FACE,{"disambiguationData":[TD([[makeQuery(id+"F4.imprint","IMPRINT",EDGE,{"disambiguationData":[TD([[subQ2,-1.0]])],"derivedFrom":subQ1}),-1.0]])]});}
            var Q11;
            {var subQ0=sQuery(id+"F4.wireOp",EDGE,"E83.MirrorCS");var subQ1=sQuery(id+"F4.wireOp",EDGE,"E79.MirrorCS");var subQ2=makeQuery(id+"F4.imprint","INTERSECT",VERTEX,{"derivedFrom":[subQ1,subQ0]});Q11=makeQuery(id+"F4.imprint","IMPRINT",FACE,{"disambiguationData":[TD([[makeQuery(id+"F4.imprint","IMPRINT",EDGE,{"disambiguationData":[TD([[subQ2,1.0]])],"derivedFrom":subQ1}),-1.0]])]});}
            var Q12;
            {var subQ0=sQuery(id+"F4.wireOp",EDGE,"E84.MirrorCS");var subQ1=sQuery(id+"F4.wireOp",EDGE,"E82.MirrorCS");var subQ2=makeQuery(id+"F4.imprint","INTERSECT",VERTEX,{"derivedFrom":[subQ1,subQ0]});Q12=makeQuery(id+"F4.imprint","IMPRINT",FACE,{"disambiguationData":[TD([[makeQuery(id+"F4.imprint","IMPRINT",EDGE,{"disambiguationData":[TD([[subQ2,-1.0]])],"derivedFrom":subQ1}),1.0]])]});}
            var Q13;
            {var subQ0=sQuery(id+"F4.wireOp",EDGE,"E91.MirrorCS");var subQ1=sQuery(id+"F4.wireOp",EDGE,"E84.MirrorCS");var subQ2=makeQuery(id+"F4.imprint","INTERSECT",VERTEX,{"derivedFrom":[subQ1,subQ0]});Q13=makeQuery(id+"F4.imprint","IMPRINT",FACE,{"disambiguationData":[TD([[makeQuery(id+"F4.imprint","IMPRINT",EDGE,{"disambiguationData":[TD([[subQ2,-1.0]])],"derivedFrom":subQ1}),-1.0]])]});}
            var Q14;
            {var subQ0=sQuery(id+"F4.wireOp",EDGE,"E89.MirrorCS");var subQ1=sQuery(id+"F4.wireOp",EDGE,"E79.MirrorCS");var subQ2=makeQuery(id+"F4.imprint","INTERSECT",VERTEX,{"derivedFrom":[subQ1,subQ0]});Q14=makeQuery(id+"F4.imprint","IMPRINT",FACE,{"disambiguationData":[TD([[makeQuery(id+"F4.imprint","IMPRINT",EDGE,{"disambiguationData":[TD([[subQ2,-1.0]])],"derivedFrom":subQ1}),-1.0]])]});}
            var Q15;
            {var subQ0=sQuery(id+"F4.wireOp",EDGE,"E89.MirrorCS");var subQ1=sQuery(id+"F4.wireOp",EDGE,"E84.MirrorCS");var subQ2=makeQuery(id+"F4.imprint","INTERSECT",VERTEX,{"derivedFrom":[subQ1,subQ0]});Q15=makeQuery(id+"F4.imprint","IMPRINT",FACE,{"disambiguationData":[TD([[makeQuery(id+"F4.imprint","IMPRINT",EDGE,{"disambiguationData":[TD([[subQ2,-1.0]])],"derivedFrom":subQ1}),-1.0]])]});}
            var Q16;
            {var subQ0=sQuery(id+"F4.wireOp",EDGE,"E70.bottom");var subQ1=sQuery(id+"F4.wireOp",EDGE,"E58.left");var subQ2=makeQuery(id+"F4.imprint","INTERSECT",VERTEX,{"derivedFrom":[subQ1,subQ0]});Q16=makeQuery(id+"F4.imprint","IMPRINT",FACE,{"disambiguationData":[TD([[makeQuery(id+"F4.imprint","IMPRINT",EDGE,{"disambiguationData":[TD([[subQ2,-1.0]])],"derivedFrom":subQ1}),1.0]])]});}
            var Q17;
            {var subQ0=sQuery(id+"F4.wireOp",EDGE,"E68.bottom");var subQ1=sQuery(id+"F4.wireOp",EDGE,"E58.left");var subQ2=makeQuery(id+"F4.imprint","INTERSECT",VERTEX,{"derivedFrom":[subQ1,subQ0]});Q17=makeQuery(id+"F4.imprint","IMPRINT",FACE,{"disambiguationData":[TD([[makeQuery(id+"F4.imprint","IMPRINT",EDGE,{"disambiguationData":[TD([[subQ2,-1.0]])],"derivedFrom":subQ1}),1.0]])]});}
            extrude(context, id + "F5", {"entities" : qUnion([Q0, Q1, Q2, Q3, Q4, Q5, Q6, Q7, Q8, Q9, Q10, Q11, Q12, Q13, Q14, Q15, Q16, Q17]), "operationType" : NewBodyOperationType.ADD, "endBound" : BoundingType.SYMMETRIC, "depth" : 1 * mm});
        }
        {
            var Q0;
            {var subQ5=sQuery(id+"F4.wireOp",EDGE,"E66.left");Q0=makeQuery(id+"F4.imprint","IMPRINT",FACE,{"disambiguationData":[TD([[makeQuery(id+"F4.imprint","IMPRINT",EDGE,{"derivedFrom":subQ5}),1.0]])]});}
            var Q1;
            {var subQ0=sQuery(id+"F4.wireOp",EDGE,"E66.bottom");var subQ1=sQuery(id+"F4.wireOp",EDGE,"E62.MirrorCS");var subQ2=makeQuery(id+"F4.imprint","INTERSECT",VERTEX,{"derivedFrom":[subQ1,subQ0]});Q1=makeQuery(id+"F4.imprint","IMPRINT",FACE,{"disambiguationData":[TD([[makeQuery(id+"F4.imprint","IMPRINT",EDGE,{"disambiguationData":[TD([[subQ2,1.0]])],"derivedFrom":subQ1}),1.0]])]});}
            var Q2;
            {var subQ0=sQuery(id+"F4.wireOp",EDGE,"E66.bottom");var subQ1=sQuery(id+"F4.wireOp",EDGE,"E58.right");var subQ2=makeQuery(id+"F4.imprint","INTERSECT",VERTEX,{"derivedFrom":[subQ1,subQ0]});Q2=makeQuery(id+"F4.imprint","IMPRINT",FACE,{"disambiguationData":[TD([[makeQuery(id+"F4.imprint","IMPRINT",EDGE,{"disambiguationData":[TD([[subQ2,1.0]])],"derivedFrom":subQ1}),1.0]])]});}
            var Q3;
            {var subQ0=sQuery(id+"F4.wireOp",EDGE,"E66.bottom");var subQ1=sQuery(id+"F4.wireOp",EDGE,"E58.left");var subQ2=makeQuery(id+"F4.imprint","INTERSECT",VERTEX,{"derivedFrom":[subQ1,subQ0]});Q3=makeQuery(id+"F4.imprint","IMPRINT",FACE,{"disambiguationData":[TD([[makeQuery(id+"F4.imprint","IMPRINT",EDGE,{"disambiguationData":[TD([[subQ2,1.0]])],"derivedFrom":subQ1}),1.0]])]});}
            var Q4;
            {var subQ0=sQuery(id+"F4.wireOp",EDGE,"E66.bottom");var subQ1=sQuery(id+"F4.wireOp",EDGE,"E58.left");var subQ2=makeQuery(id+"F4.imprint","INTERSECT",VERTEX,{"derivedFrom":[subQ1,subQ0]});Q4=makeQuery(id+"F4.imprint","IMPRINT",FACE,{"disambiguationData":[TD([[makeQuery(id+"F4.imprint","IMPRINT",EDGE,{"disambiguationData":[TD([[subQ2,1.0]])],"derivedFrom":subQ1}),-1.0]])]});}
            var Q5;
            {var subQ0=sQuery(id+"F4.wireOp",EDGE,"E66.bottom");var subQ1=sQuery(id+"F4.wireOp",EDGE,"E60.left");var subQ2=makeQuery(id+"F4.imprint","INTERSECT",VERTEX,{"derivedFrom":[subQ1,subQ0]});Q5=makeQuery(id+"F4.imprint","IMPRINT",FACE,{"disambiguationData":[TD([[makeQuery(id+"F4.imprint","IMPRINT",EDGE,{"disambiguationData":[TD([[subQ2,1.0]])],"derivedFrom":subQ1}),-1.0]])]});}
            var Q6;
            {var subQ5=sQuery(id+"F4.wireOp",EDGE,"E66.right");Q6=makeQuery(id+"F4.imprint","IMPRINT",FACE,{"disambiguationData":[TD([[makeQuery(id+"F4.imprint","IMPRINT",EDGE,{"derivedFrom":subQ5}),-1.0]])]});}
            var Q7;
            {var subQ5=sQuery(id+"F4.wireOp",EDGE,"E68.right");Q7=makeQuery(id+"F4.imprint","IMPRINT",FACE,{"disambiguationData":[TD([[makeQuery(id+"F4.imprint","IMPRINT",EDGE,{"derivedFrom":subQ5}),-1.0]])]});}
            var Q8;
            {var subQ0=sQuery(id+"F4.wireOp",EDGE,"E68.top");var subQ1=sQuery(id+"F4.wireOp",EDGE,"E60.left");var subQ2=makeQuery(id+"F4.imprint","INTERSECT",VERTEX,{"derivedFrom":[subQ1,subQ0]});Q8=makeQuery(id+"F4.imprint","IMPRINT",FACE,{"disambiguationData":[TD([[makeQuery(id+"F4.imprint","IMPRINT",EDGE,{"disambiguationData":[TD([[subQ2,-1.0]])],"derivedFrom":subQ1}),-1.0]])]});}
            var Q9;
            {var subQ0=sQuery(id+"F4.wireOp",EDGE,"E68.top");var subQ1=sQuery(id+"F4.wireOp",EDGE,"E58.left");var subQ2=makeQuery(id+"F4.imprint","INTERSECT",VERTEX,{"derivedFrom":[subQ1,subQ0]});Q9=makeQuery(id+"F4.imprint","IMPRINT",FACE,{"disambiguationData":[TD([[makeQuery(id+"F4.imprint","IMPRINT",EDGE,{"disambiguationData":[TD([[subQ2,-1.0]])],"derivedFrom":subQ1}),-1.0]])]});}
            var Q10;
            {var subQ0=sQuery(id+"F4.wireOp",EDGE,"E68.top");var subQ1=sQuery(id+"F4.wireOp",EDGE,"E58.left");var subQ2=makeQuery(id+"F4.imprint","INTERSECT",VERTEX,{"derivedFrom":[subQ1,subQ0]});Q10=makeQuery(id+"F4.imprint","IMPRINT",FACE,{"disambiguationData":[TD([[makeQuery(id+"F4.imprint","IMPRINT",EDGE,{"disambiguationData":[TD([[subQ2,-1.0]])],"derivedFrom":subQ1}),1.0]])]});}
            var Q11;
            {var subQ0=sQuery(id+"F4.wireOp",EDGE,"E68.top");var subQ1=sQuery(id+"F4.wireOp",EDGE,"E58.right");var subQ2=makeQuery(id+"F4.imprint","INTERSECT",VERTEX,{"derivedFrom":[subQ1,subQ0]});Q11=makeQuery(id+"F4.imprint","IMPRINT",FACE,{"disambiguationData":[TD([[makeQuery(id+"F4.imprint","IMPRINT",EDGE,{"disambiguationData":[TD([[subQ2,-1.0]])],"derivedFrom":subQ1}),1.0]])]});}
            var Q12;
            {var subQ0=sQuery(id+"F4.wireOp",EDGE,"E68.top");var subQ1=sQuery(id+"F4.wireOp",EDGE,"E62.MirrorCS");var subQ2=makeQuery(id+"F4.imprint","INTERSECT",VERTEX,{"derivedFrom":[subQ1,subQ0]});Q12=makeQuery(id+"F4.imprint","IMPRINT",FACE,{"disambiguationData":[TD([[makeQuery(id+"F4.imprint","IMPRINT",EDGE,{"disambiguationData":[TD([[subQ2,-1.0]])],"derivedFrom":subQ1}),1.0]])]});}
            var Q13;
            {var subQ5=sQuery(id+"F4.wireOp",EDGE,"E68.left");Q13=makeQuery(id+"F4.imprint","IMPRINT",FACE,{"disambiguationData":[TD([[makeQuery(id+"F4.imprint","IMPRINT",EDGE,{"derivedFrom":subQ5}),1.0]])]});}
            var Q14;
            {var subQ5=sQuery(id+"F4.wireOp",EDGE,"E70.left");Q14=makeQuery(id+"F4.imprint","IMPRINT",FACE,{"disambiguationData":[TD([[makeQuery(id+"F4.imprint","IMPRINT",EDGE,{"derivedFrom":subQ5}),1.0]])]});}
            var Q15;
            {var subQ0=sQuery(id+"F4.wireOp",EDGE,"E70.top");var subQ1=sQuery(id+"F4.wireOp",EDGE,"E62.MirrorCS");var subQ2=makeQuery(id+"F4.imprint","INTERSECT",VERTEX,{"derivedFrom":[subQ1,subQ0]});Q15=makeQuery(id+"F4.imprint","IMPRINT",FACE,{"disambiguationData":[TD([[makeQuery(id+"F4.imprint","IMPRINT",EDGE,{"disambiguationData":[TD([[subQ2,-1.0]])],"derivedFrom":subQ1}),1.0]])]});}
            var Q16;
            {var subQ0=sQuery(id+"F4.wireOp",EDGE,"E70.top");var subQ1=sQuery(id+"F4.wireOp",EDGE,"E58.right");var subQ2=makeQuery(id+"F4.imprint","INTERSECT",VERTEX,{"derivedFrom":[subQ1,subQ0]});Q16=makeQuery(id+"F4.imprint","IMPRINT",FACE,{"disambiguationData":[TD([[makeQuery(id+"F4.imprint","IMPRINT",EDGE,{"disambiguationData":[TD([[subQ2,-1.0]])],"derivedFrom":subQ1}),1.0]])]});}
            var Q17;
            {var subQ0=sQuery(id+"F4.wireOp",EDGE,"E70.top");var subQ1=sQuery(id+"F4.wireOp",EDGE,"E58.left");var subQ2=makeQuery(id+"F4.imprint","INTERSECT",VERTEX,{"derivedFrom":[subQ1,subQ0]});Q17=makeQuery(id+"F4.imprint","IMPRINT",FACE,{"disambiguationData":[TD([[makeQuery(id+"F4.imprint","IMPRINT",EDGE,{"disambiguationData":[TD([[subQ2,-1.0]])],"derivedFrom":subQ1}),1.0]])]});}
            var Q18;
            {var subQ0=sQuery(id+"F4.wireOp",EDGE,"E70.top");var subQ1=sQuery(id+"F4.wireOp",EDGE,"E58.left");var subQ2=makeQuery(id+"F4.imprint","INTERSECT",VERTEX,{"derivedFrom":[subQ1,subQ0]});Q18=makeQuery(id+"F4.imprint","IMPRINT",FACE,{"disambiguationData":[TD([[makeQuery(id+"F4.imprint","IMPRINT",EDGE,{"disambiguationData":[TD([[subQ2,-1.0]])],"derivedFrom":subQ1}),-1.0]])]});}
            var Q19;
            {var subQ0=sQuery(id+"F4.wireOp",EDGE,"E70.top");var subQ1=sQuery(id+"F4.wireOp",EDGE,"E60.left");var subQ2=makeQuery(id+"F4.imprint","INTERSECT",VERTEX,{"derivedFrom":[subQ1,subQ0]});Q19=makeQuery(id+"F4.imprint","IMPRINT",FACE,{"disambiguationData":[TD([[makeQuery(id+"F4.imprint","IMPRINT",EDGE,{"disambiguationData":[TD([[subQ2,-1.0]])],"derivedFrom":subQ1}),-1.0]])]});}
            var Q20;
            {var subQ5=sQuery(id+"F4.wireOp",EDGE,"E70.right");Q20=makeQuery(id+"F4.imprint","IMPRINT",FACE,{"disambiguationData":[TD([[makeQuery(id+"F4.imprint","IMPRINT",EDGE,{"derivedFrom":subQ5}),-1.0]])]});}
            var Q21;
            {var subQ0=sQuery(id+"F4.wireOp",EDGE,"E88.MirrorCS");Q21=makeQuery(id+"F4.imprint","IMPRINT",FACE,{"disambiguationData":[TD([[makeQuery(id+"F4.imprint","IMPRINT",EDGE,{"derivedFrom":subQ0}),1.0]])]});}
            var Q22;
            {var subQ0=sQuery(id+"F4.wireOp",EDGE,"E83.MirrorCS");var subQ1=sQuery(id+"F4.wireOp",EDGE,"E79.MirrorCS");var subQ2=makeQuery(id+"F4.imprint","INTERSECT",VERTEX,{"derivedFrom":[subQ1,subQ0]});Q22=makeQuery(id+"F4.imprint","IMPRINT",FACE,{"disambiguationData":[TD([[makeQuery(id+"F4.imprint","IMPRINT",EDGE,{"disambiguationData":[TD([[subQ2,1.0]])],"derivedFrom":subQ1}),1.0]])]});}
            var Q23;
            {var subQ0=sQuery(id+"F4.wireOp",EDGE,"E86.MirrorCS");var subQ1=sQuery(id+"F4.wireOp",EDGE,"E79.MirrorCS");var subQ2=makeQuery(id+"F4.imprint","INTERSECT",VERTEX,{"derivedFrom":[subQ1,subQ0]});Q23=makeQuery(id+"F4.imprint","IMPRINT",FACE,{"disambiguationData":[TD([[makeQuery(id+"F4.imprint","IMPRINT",EDGE,{"disambiguationData":[TD([[subQ2,-1.0]])],"derivedFrom":subQ1}),1.0]])]});}
            var Q24;
            {var subQ0=sQuery(id+"F4.wireOp",EDGE,"E89.MirrorCS");var subQ1=sQuery(id+"F4.wireOp",EDGE,"E79.MirrorCS");var subQ2=makeQuery(id+"F4.imprint","INTERSECT",VERTEX,{"derivedFrom":[subQ1,subQ0]});Q24=makeQuery(id+"F4.imprint","IMPRINT",FACE,{"disambiguationData":[TD([[makeQuery(id+"F4.imprint","IMPRINT",EDGE,{"disambiguationData":[TD([[subQ2,-1.0]])],"derivedFrom":subQ1}),1.0]])]});}
            var Q25;
            {var subQ0=sQuery(id+"F4.wireOp",EDGE,"E90.MirrorCS");var subQ1=sQuery(id+"F4.wireOp",EDGE,"E79.MirrorCS");var subQ2=makeQuery(id+"F4.imprint","INTERSECT",VERTEX,{"derivedFrom":[subQ1,subQ0]});Q25=makeQuery(id+"F4.imprint","IMPRINT",FACE,{"disambiguationData":[TD([[makeQuery(id+"F4.imprint","IMPRINT",EDGE,{"disambiguationData":[TD([[subQ2,-1.0]])],"derivedFrom":subQ1}),1.0]])]});}
            var Q26;
            {var subQ0=sQuery(id+"F4.wireOp",EDGE,"E91.MirrorCS");var subQ1=sQuery(id+"F4.wireOp",EDGE,"E79.MirrorCS");var subQ2=makeQuery(id+"F4.imprint","INTERSECT",VERTEX,{"derivedFrom":[subQ1,subQ0]});Q26=makeQuery(id+"F4.imprint","IMPRINT",FACE,{"disambiguationData":[TD([[makeQuery(id+"F4.imprint","IMPRINT",EDGE,{"disambiguationData":[TD([[subQ2,-1.0]])],"derivedFrom":subQ1}),1.0]])]});}
            var Q27;
            {var subQ0=sQuery(id+"F4.wireOp",EDGE,"E100.MirrorCS");Q27=makeQuery(id+"F4.imprint","IMPRINT",FACE,{"disambiguationData":[TD([[makeQuery(id+"F4.imprint","IMPRINT",EDGE,{"derivedFrom":subQ0}),-1.0]])]});}
            var Q28;
            {var subQ0=sQuery(id+"F4.wireOp",EDGE,"E101.MirrorCS");Q28=makeQuery(id+"F4.imprint","IMPRINT",FACE,{"disambiguationData":[TD([[makeQuery(id+"F4.imprint","IMPRINT",EDGE,{"derivedFrom":subQ0}),-1.0]])]});}
            var Q29;
            {var subQ0=sQuery(id+"F4.wireOp",EDGE,"E91.MirrorCS");var subQ1=sQuery(id+"F4.wireOp",EDGE,"E84.MirrorCS");var subQ2=makeQuery(id+"F4.imprint","INTERSECT",VERTEX,{"derivedFrom":[subQ1,subQ0]});Q29=makeQuery(id+"F4.imprint","IMPRINT",FACE,{"disambiguationData":[TD([[makeQuery(id+"F4.imprint","IMPRINT",EDGE,{"disambiguationData":[TD([[subQ2,-1.0]])],"derivedFrom":subQ1}),1.0]])]});}
            var Q30;
            {var subQ0=sQuery(id+"F4.wireOp",EDGE,"E90.MirrorCS");var subQ1=sQuery(id+"F4.wireOp",EDGE,"E84.MirrorCS");var subQ2=makeQuery(id+"F4.imprint","INTERSECT",VERTEX,{"derivedFrom":[subQ1,subQ0]});Q30=makeQuery(id+"F4.imprint","IMPRINT",FACE,{"disambiguationData":[TD([[makeQuery(id+"F4.imprint","IMPRINT",EDGE,{"disambiguationData":[TD([[subQ2,-1.0]])],"derivedFrom":subQ1}),1.0]])]});}
            var Q31;
            {var subQ0=sQuery(id+"F4.wireOp",EDGE,"E89.MirrorCS");var subQ1=sQuery(id+"F4.wireOp",EDGE,"E84.MirrorCS");var subQ2=makeQuery(id+"F4.imprint","INTERSECT",VERTEX,{"derivedFrom":[subQ1,subQ0]});Q31=makeQuery(id+"F4.imprint","IMPRINT",FACE,{"disambiguationData":[TD([[makeQuery(id+"F4.imprint","IMPRINT",EDGE,{"disambiguationData":[TD([[subQ2,-1.0]])],"derivedFrom":subQ1}),1.0]])]});}
            var Q32;
            {var subQ0=sQuery(id+"F4.wireOp",EDGE,"E94.MirrorCS");var subQ1=sQuery(id+"F4.wireOp",EDGE,"E82.MirrorCS");var subQ2=makeQuery(id+"F4.imprint","INTERSECT",VERTEX,{"derivedFrom":[subQ1,subQ0]});Q32=makeQuery(id+"F4.imprint","IMPRINT",FACE,{"disambiguationData":[TD([[makeQuery(id+"F4.imprint","IMPRINT",EDGE,{"disambiguationData":[TD([[subQ2,-1.0]])],"derivedFrom":subQ1}),-1.0]])]});}
            var Q33;
            {var subQ0=sQuery(id+"F4.wireOp",EDGE,"E94.MirrorCS");var subQ1=sQuery(id+"F4.wireOp",EDGE,"E82.MirrorCS");var subQ2=makeQuery(id+"F4.imprint","INTERSECT",VERTEX,{"derivedFrom":[subQ1,subQ0]});Q33=makeQuery(id+"F4.imprint","IMPRINT",FACE,{"disambiguationData":[TD([[makeQuery(id+"F4.imprint","IMPRINT",EDGE,{"disambiguationData":[TD([[subQ2,-1.0]])],"derivedFrom":subQ1}),1.0]])]});}
            var Q34;
            {var subQ5=sQuery(id+"F4.wireOp",EDGE,"E85.MirrorCS");Q34=makeQuery(id+"F4.imprint","IMPRINT",FACE,{"disambiguationData":[TD([[makeQuery(id+"F4.imprint","IMPRINT",EDGE,{"derivedFrom":subQ5}),1.0]])]});}
            var Q35;
            {var subQ5=sQuery(id+"F4.wireOp",EDGE,"E96.MirrorCS");Q35=makeQuery(id+"F4.imprint","IMPRINT",FACE,{"disambiguationData":[TD([[makeQuery(id+"F4.imprint","IMPRINT",EDGE,{"derivedFrom":subQ5}),1.0]])]});}
            var Q36;
            {var subQ0=sQuery(id+"F4.wireOp",EDGE,"E92.MirrorCS");var subQ1=sQuery(id+"F4.wireOp",EDGE,"E82.MirrorCS");var subQ2=makeQuery(id+"F4.imprint","INTERSECT",VERTEX,{"derivedFrom":[subQ1,subQ0]});Q36=makeQuery(id+"F4.imprint","IMPRINT",FACE,{"disambiguationData":[TD([[makeQuery(id+"F4.imprint","IMPRINT",EDGE,{"disambiguationData":[TD([[subQ2,1.0]])],"derivedFrom":subQ1}),1.0]])]});}
            var Q37;
            {var subQ0=sQuery(id+"F4.wireOp",EDGE,"E92.MirrorCS");var subQ1=sQuery(id+"F4.wireOp",EDGE,"E82.MirrorCS");var subQ2=makeQuery(id+"F4.imprint","INTERSECT",VERTEX,{"derivedFrom":[subQ1,subQ0]});Q37=makeQuery(id+"F4.imprint","IMPRINT",FACE,{"disambiguationData":[TD([[makeQuery(id+"F4.imprint","IMPRINT",EDGE,{"disambiguationData":[TD([[subQ2,1.0]])],"derivedFrom":subQ1}),-1.0]])]});}
            var Q38;
            {var subQ0=sQuery(id+"F4.wireOp",EDGE,"E92.MirrorCS");var subQ1=sQuery(id+"F4.wireOp",EDGE,"E86.MirrorCS");var subQ2=makeQuery(id+"F4.imprint","INTERSECT",VERTEX,{"derivedFrom":[subQ1,subQ0]});Q38=makeQuery(id+"F4.imprint","IMPRINT",FACE,{"disambiguationData":[TD([[makeQuery(id+"F4.imprint","IMPRINT",EDGE,{"disambiguationData":[TD([[subQ2,1.0]])],"derivedFrom":subQ1}),-1.0]])]});}
            var Q39;
            {var subQ0=sQuery(id+"F4.wireOp",EDGE,"E92.MirrorCS");var subQ1=sQuery(id+"F4.wireOp",EDGE,"E90.MirrorCS");var subQ2=makeQuery(id+"F4.imprint","INTERSECT",VERTEX,{"derivedFrom":[subQ1,subQ0]});Q39=makeQuery(id+"F4.imprint","IMPRINT",FACE,{"disambiguationData":[TD([[makeQuery(id+"F4.imprint","IMPRINT",EDGE,{"disambiguationData":[TD([[subQ2,1.0]])],"derivedFrom":subQ1}),-1.0]])]});}
            var Q40;
            {var subQ0=sQuery(id+"F4.wireOp",EDGE,"E80.MirrorCS");Q40=makeQuery(id+"F4.imprint","IMPRINT",FACE,{"disambiguationData":[TD([[makeQuery(id+"F4.imprint","IMPRINT",EDGE,{"derivedFrom":subQ0}),-1.0]])]});}
            var Q41;
            {var subQ0=sQuery(id+"F4.wireOp",EDGE,"E92.MirrorCS");var subQ1=sQuery(id+"F4.wireOp",EDGE,"E89.MirrorCS");var subQ2=makeQuery(id+"F4.imprint","INTERSECT",VERTEX,{"derivedFrom":[subQ1,subQ0]});Q41=makeQuery(id+"F4.imprint","IMPRINT",FACE,{"disambiguationData":[TD([[makeQuery(id+"F4.imprint","IMPRINT",EDGE,{"disambiguationData":[TD([[subQ2,1.0]])],"derivedFrom":subQ1}),-1.0]])]});}
            extrude(context, id + "F6", {"entities" : qUnion([Q0, Q1, Q2, Q3, Q4, Q5, Q6, Q7, Q8, Q9, Q10, Q11, Q12, Q13, Q14, Q15, Q16, Q17, Q18, Q19, Q20, Q21, Q22, Q23, Q24, Q25, Q26, Q27, Q28, Q29, Q30, Q31, Q32, Q33, Q34, Q35, Q36, Q37, Q38, Q39, Q40, Q41]), "endBound" : BoundingType.SYMMETRIC, "depth" : 2 * mm});
        }
        {
            var Q0;
            Q0=makeQuery(id+"F6.opExtrude","SWEPT_BODY",BODY,{"disambiguationData":[OSD([sQuery(id+"F4.wireOp",EDGE,"E70.bottom"),sQuery(id+"F4.wireOp",EDGE,"E70.top"),sQuery(id+"F4.wireOp",EDGE,"E70.left"),sQuery(id+"F4.wireOp",EDGE,"E70.right")])]});
            var Q1;
            Q1=makeQuery(id+"F6.opExtrude","SWEPT_BODY",BODY,{"disambiguationData":[OSD([sQuery(id+"F4.wireOp",EDGE,"E66.bottom"),sQuery(id+"F4.wireOp",EDGE,"E66.top"),sQuery(id+"F4.wireOp",EDGE,"E66.left"),sQuery(id+"F4.wireOp",EDGE,"E66.right")])]});
            var Q2;
            Q2=makeQuery(id+"F5.opExtrude","SWEPT_BODY",BODY,{"disambiguationData":[OSD([sQuery(id+"F4.wireOp",EDGE,"E74.MirrorCS"),sQuery(id+"F4.wireOp",EDGE,"E90.MirrorCS"),sQuery(id+"F4.wireOp",EDGE,"E91.MirrorCS"),sQuery(id+"F4.wireOp",EDGE,"E102.MirrorCS")])]});
            var Q3;
            Q3=makeQuery(id+"F5.opExtrude","SWEPT_BODY",BODY,{"disambiguationData":[OSD([sQuery(id+"F4.wireOp",EDGE,"E62.MirrorCS"),sQuery(id+"F4.wireOp",EDGE,"E63.MirrorCS"),sQuery(id+"F4.wireOp",EDGE,"E70.top"),sQuery(id+"F4.wireOp",EDGE,"E71")])]});
            var Q4;
            Q4=makeQuery(id+"F5.opExtrude","SWEPT_BODY",BODY,{"disambiguationData":[OSD([sQuery(id+"F4.wireOp",EDGE,"E58.bottom"),sQuery(id+"F4.wireOp",EDGE,"E58.left"),sQuery(id+"F4.wireOp",EDGE,"E58.right"),sQuery(id+"F4.wireOp",EDGE,"E70.top")])]});
            var Q5;
            Q5=makeQuery(id+"F3.opExtrude","SWEPT_BODY",BODY,{"disambiguationData":[OSD([sQuery(id+"F0.wireOp",EDGE,"E32.MirrorCS"),sQuery(id+"F0.wireOp",EDGE,"E36.MirrorCS"),sQuery(id+"F0.wireOp",EDGE,"E40.MirrorCS"),sQuery(id+"F0.wireOp",EDGE,"E53.MirrorCS")])]});
            var Q6;
            Q6=makeQuery(id+"F3.opExtrude","SWEPT_BODY",BODY,{"disambiguationData":[OSD([sQuery(id+"F0.wireOp",EDGE,"E29.MirrorCS"),sQuery(id+"F0.wireOp",EDGE,"E41.MirrorCS"),sQuery(id+"F0.wireOp",EDGE,"E45.MirrorCS"),sQuery(id+"F0.wireOp",EDGE,"E48.MirrorCS")])]});
            var Q7;
            Q7=makeQuery(id+"F3.opExtrude","SWEPT_BODY",BODY,{"disambiguationData":[OSD([sQuery(id+"F0.wireOp",EDGE,"E21.bottom"),sQuery(id+"F0.wireOp",EDGE,"E21.top"),sQuery(id+"F0.wireOp",EDGE,"E21.left"),sQuery(id+"F0.wireOp",EDGE,"E21.right")])]});
            var Q8;
            Q8=makeQuery(id+"F3.opExtrude","SWEPT_BODY",BODY,{"disambiguationData":[OSD([sQuery(id+"F0.wireOp",EDGE,"E19.bottom"),sQuery(id+"F0.wireOp",EDGE,"E19.top"),sQuery(id+"F0.wireOp",EDGE,"E19.left"),sQuery(id+"F0.wireOp",EDGE,"E19.right")])]});
            var Q9;
            Q9=makeQuery(id+"F2.opExtrude","SWEPT_BODY",BODY,{"disambiguationData":[OSD([sQuery(id+"F0.wireOp",EDGE,"E13.MirrorCS"),sQuery(id+"F0.wireOp",EDGE,"E14.MirrorCS"),sQuery(id+"F0.wireOp",EDGE,"E15.MirrorCS"),sQuery(id+"F0.wireOp",EDGE,"E21.top")])]});
            var Q10;
            Q10=makeQuery(id+"F6.opExtrude","SWEPT_BODY",BODY,{"disambiguationData":[OSD([sQuery(id+"F4.wireOp",EDGE,"E84.MirrorCS"),sQuery(id+"F4.wireOp",EDGE,"E85.MirrorCS"),sQuery(id+"F4.wireOp",EDGE,"E94.MirrorCS"),sQuery(id+"F4.wireOp",EDGE,"E101.MirrorCS")])]});
            var Q11;
            Q11=makeQuery(id+"F2.opExtrude","SWEPT_BODY",BODY,{"disambiguationData":[OSD([sQuery(id+"F0.wireOp",EDGE,"E3.MirrorCS"),sQuery(id+"F0.wireOp",EDGE,"E37.MirrorCS"),sQuery(id+"F0.wireOp",EDGE,"E40.MirrorCS"),sQuery(id+"F0.wireOp",EDGE,"E46.MirrorCS")])]});
            var Q12;
            Q12=makeQuery(id+"F2.opExtrude","SWEPT_BODY",BODY,{"disambiguationData":[OSD([sQuery(id+"F0.wireOp",EDGE,"E8.bottom"),sQuery(id+"F0.wireOp",EDGE,"E8.left"),sQuery(id+"F0.wireOp",EDGE,"E8.right"),sQuery(id+"F0.wireOp",EDGE,"E21.top")])]});
            var Q13;
            Q13=makeQuery(id+"F2.opExtrude","SWEPT_BODY",BODY,{"disambiguationData":[OSD([sQuery(id+"F0.wireOp",EDGE,"E3.MirrorCS"),sQuery(id+"F0.wireOp",EDGE,"E31.MirrorCS"),sQuery(id+"F0.wireOp",EDGE,"E34.MirrorCS"),sQuery(id+"F0.wireOp",EDGE,"E40.MirrorCS")])]});
            var Q14;
            Q14=makeQuery(id+"F1.opRevolve","SWEPT_BODY",BODY,{"disambiguationData":[OSD([sQuery(id+"F0.wireOp",EDGE,"E1.right"),sQuery(id+"F0.wireOp",EDGE,"E3.MirrorCS"),sQuery(id+"F0.wireOp",EDGE,"E4.MirrorCS"),sQuery(id+"F0.wireOp",EDGE,"E22.MirrorCS"),sQuery(id+"F0.wireOp",EDGE,"E7.MirrorCS"),sQuery(id+"F0.wireOp",EDGE,"E24.MirrorCS"),sQuery(id+"F0.wireOp",EDGE,"E25.MirrorCS"),sQuery(id+"F0.wireOp",EDGE,"E56")])]});
            var Q15;
            Q15=makeQuery(id+"F6.opExtrude","SWEPT_BODY",BODY,{"disambiguationData":[OSD([sQuery(id+"F4.wireOp",EDGE,"E79.MirrorCS"),sQuery(id+"F4.wireOp",EDGE,"E88.MirrorCS"),sQuery(id+"F4.wireOp",EDGE,"E100.MirrorCS"),sQuery(id+"F4.wireOp",EDGE,"E102.MirrorCS")])]});
            var Q16;
            Q16=makeQuery(id+"F6.opExtrude","SWEPT_BODY",BODY,{"disambiguationData":[OSD([sQuery(id+"F4.wireOp",EDGE,"E80.MirrorCS"),sQuery(id+"F4.wireOp",EDGE,"E92.MirrorCS"),sQuery(id+"F4.wireOp",EDGE,"E96.MirrorCS"),sQuery(id+"F4.wireOp",EDGE,"E103.MirrorCS")])]});
            var Q17;
            Q17=makeQuery(id+"F6.opExtrude","SWEPT_BODY",BODY,{"disambiguationData":[OSD([sQuery(id+"F4.wireOp",EDGE,"E68.bottom"),sQuery(id+"F4.wireOp",EDGE,"E68.top"),sQuery(id+"F4.wireOp",EDGE,"E68.left"),sQuery(id+"F4.wireOp",EDGE,"E68.right")])]});
            var Q18;
            Q18=makeQuery(id+"F5.opExtrude","SWEPT_BODY",BODY,{"disambiguationData":[OSD([sQuery(id+"F4.wireOp",EDGE,"E79.MirrorCS"),sQuery(id+"F4.wireOp",EDGE,"E90.MirrorCS"),sQuery(id+"F4.wireOp",EDGE,"E91.MirrorCS"),sQuery(id+"F4.wireOp",EDGE,"E94.MirrorCS")])]});
            var Q19;
            Q19=makeQuery(id+"F5.opExtrude","SWEPT_BODY",BODY,{"disambiguationData":[OSD([sQuery(id+"F4.wireOp",EDGE,"E77.MirrorCS"),sQuery(id+"F4.wireOp",EDGE,"E86.MirrorCS"),sQuery(id+"F4.wireOp",EDGE,"E89.MirrorCS"),sQuery(id+"F4.wireOp",EDGE,"E102.MirrorCS")])]});
            var Q20;
            Q20=makeQuery(id+"F5.opExtrude","SWEPT_BODY",BODY,{"disambiguationData":[OSD([sQuery(id+"F4.wireOp",EDGE,"E75.MirrorCS"),sQuery(id+"F4.wireOp",EDGE,"E82.MirrorCS"),sQuery(id+"F4.wireOp",EDGE,"E83.MirrorCS"),sQuery(id+"F4.wireOp",EDGE,"E102.MirrorCS")])]});
            var Q21;
            Q21=makeQuery(id+"F5.opExtrude","SWEPT_BODY",BODY,{"disambiguationData":[OSD([sQuery(id+"F4.wireOp",EDGE,"E62.MirrorCS"),sQuery(id+"F4.wireOp",EDGE,"E63.MirrorCS"),sQuery(id+"F4.wireOp",EDGE,"E68.top"),sQuery(id+"F4.wireOp",EDGE,"E70.bottom")])]});
            var Q22;
            Q22=makeQuery(id+"F5.opExtrude","SWEPT_BODY",BODY,{"disambiguationData":[OSD([sQuery(id+"F4.wireOp",EDGE,"E60.bottom"),sQuery(id+"F4.wireOp",EDGE,"E60.left"),sQuery(id+"F4.wireOp",EDGE,"E60.right"),sQuery(id+"F4.wireOp",EDGE,"E70.top")])]});
            var Q23;
            Q23=makeQuery(id+"F3.opExtrude","SWEPT_BODY",BODY,{"disambiguationData":[OSD([sQuery(id+"F0.wireOp",EDGE,"E39.MirrorCS"),sQuery(id+"F0.wireOp",EDGE,"E44.MirrorCS"),sQuery(id+"F0.wireOp",EDGE,"E49.MirrorCS"),sQuery(id+"F0.wireOp",EDGE,"E52.MirrorCS")])]});
            var Q24;
            Q24=makeQuery(id+"F3.opExtrude","SWEPT_BODY",BODY,{"disambiguationData":[OSD([sQuery(id+"F0.wireOp",EDGE,"E17.bottom"),sQuery(id+"F0.wireOp",EDGE,"E17.top"),sQuery(id+"F0.wireOp",EDGE,"E17.left"),sQuery(id+"F0.wireOp",EDGE,"E17.right")])]});
            var Q25;
            Q25=makeQuery(id+"F2.opExtrude","SWEPT_BODY",BODY,{"disambiguationData":[OSD([sQuery(id+"F0.wireOp",EDGE,"E37.MirrorCS"),sQuery(id+"F0.wireOp",EDGE,"E41.MirrorCS"),sQuery(id+"F0.wireOp",EDGE,"E46.MirrorCS"),sQuery(id+"F0.wireOp",EDGE,"E53.MirrorCS")])]});
            var Q26;
            Q26=makeQuery(id+"F2.opExtrude","SWEPT_BODY",BODY,{"disambiguationData":[OSD([sQuery(id+"F0.wireOp",EDGE,"E31.MirrorCS"),sQuery(id+"F0.wireOp",EDGE,"E34.MirrorCS"),sQuery(id+"F0.wireOp",EDGE,"E41.MirrorCS"),sQuery(id+"F0.wireOp",EDGE,"E53.MirrorCS")])]});
            var Q27;
            Q27=makeQuery(id+"F2.opExtrude","SWEPT_BODY",BODY,{"disambiguationData":[OSD([sQuery(id+"F0.wireOp",EDGE,"E29.MirrorCS"),sQuery(id+"F0.wireOp",EDGE,"E37.MirrorCS"),sQuery(id+"F0.wireOp",EDGE,"E46.MirrorCS"),sQuery(id+"F0.wireOp",EDGE,"E49.MirrorCS")])]});
            var Q28;
            Q28=makeQuery(id+"F2.opExtrude","SWEPT_BODY",BODY,{"disambiguationData":[OSD([sQuery(id+"F0.wireOp",EDGE,"E29.MirrorCS"),sQuery(id+"F0.wireOp",EDGE,"E31.MirrorCS"),sQuery(id+"F0.wireOp",EDGE,"E34.MirrorCS"),sQuery(id+"F0.wireOp",EDGE,"E49.MirrorCS")])]});
            var Q29;
            Q29=makeQuery(id+"F2.opExtrude","SWEPT_BODY",BODY,{"disambiguationData":[OSD([sQuery(id+"F0.wireOp",EDGE,"E14.MirrorCS"),sQuery(id+"F0.wireOp",EDGE,"E15.MirrorCS"),sQuery(id+"F0.wireOp",EDGE,"E17.top"),sQuery(id+"F0.wireOp",EDGE,"E19.bottom")])]});
            var Q30;
            Q30=makeQuery(id+"F2.opExtrude","SWEPT_BODY",BODY,{"disambiguationData":[OSD([sQuery(id+"F0.wireOp",EDGE,"E14.MirrorCS"),sQuery(id+"F0.wireOp",EDGE,"E15.MirrorCS"),sQuery(id+"F0.wireOp",EDGE,"E19.top"),sQuery(id+"F0.wireOp",EDGE,"E21.bottom")])]});
            var Q31;
            Q31=makeQuery(id+"F5.opExtrude","SWEPT_BODY",BODY,{"disambiguationData":[OSD([sQuery(id+"F4.wireOp",EDGE,"E58.left"),sQuery(id+"F4.wireOp",EDGE,"E58.right"),sQuery(id+"F4.wireOp",EDGE,"E66.top"),sQuery(id+"F4.wireOp",EDGE,"E68.bottom")])]});
            var Q32;
            Q32=makeQuery(id+"F5.opExtrude","SWEPT_BODY",BODY,{"disambiguationData":[OSD([sQuery(id+"F4.wireOp",EDGE,"E58.left"),sQuery(id+"F4.wireOp",EDGE,"E58.right"),sQuery(id+"F4.wireOp",EDGE,"E68.top"),sQuery(id+"F4.wireOp",EDGE,"E70.bottom")])]});
            var Q33;
            Q33=makeQuery(id+"F2.opExtrude","SWEPT_BODY",BODY,{"disambiguationData":[OSD([sQuery(id+"F0.wireOp",EDGE,"E8.left"),sQuery(id+"F0.wireOp",EDGE,"E8.right"),sQuery(id+"F0.wireOp",EDGE,"E17.top"),sQuery(id+"F0.wireOp",EDGE,"E19.bottom")])]});
            var Q34;
            Q34=makeQuery(id+"F2.opExtrude","SWEPT_BODY",BODY,{"disambiguationData":[OSD([sQuery(id+"F0.wireOp",EDGE,"E10.bottom"),sQuery(id+"F0.wireOp",EDGE,"E10.left"),sQuery(id+"F0.wireOp",EDGE,"E10.right"),sQuery(id+"F0.wireOp",EDGE,"E21.top")])]});
            var Q35;
            Q35=makeQuery(id+"F2.opExtrude","SWEPT_BODY",BODY,{"disambiguationData":[OSD([sQuery(id+"F0.wireOp",EDGE,"E3.MirrorCS"),sQuery(id+"F0.wireOp",EDGE,"E40.MirrorCS"),sQuery(id+"F0.wireOp",EDGE,"E50.MirrorCS"),sQuery(id+"F0.wireOp",EDGE,"E54.MirrorCS")])]});
            var Q36;
            Q36=makeQuery(id+"F2.opExtrude","SWEPT_BODY",BODY,{"disambiguationData":[OSD([sQuery(id+"F0.wireOp",EDGE,"E8.left"),sQuery(id+"F0.wireOp",EDGE,"E8.right"),sQuery(id+"F0.wireOp",EDGE,"E19.top"),sQuery(id+"F0.wireOp",EDGE,"E21.bottom")])]});
            var Q37;
            Q37=makeQuery(id+"F5.opExtrude","SWEPT_BODY",BODY,{"disambiguationData":[OSD([sQuery(id+"F4.wireOp",EDGE,"E82.MirrorCS"),sQuery(id+"F4.wireOp",EDGE,"E83.MirrorCS"),sQuery(id+"F4.wireOp",EDGE,"E84.MirrorCS"),sQuery(id+"F4.wireOp",EDGE,"E103.MirrorCS")])]});
            var Q38;
            Q38=makeQuery(id+"F5.opExtrude","SWEPT_BODY",BODY,{"disambiguationData":[OSD([sQuery(id+"F4.wireOp",EDGE,"E79.MirrorCS"),sQuery(id+"F4.wireOp",EDGE,"E82.MirrorCS"),sQuery(id+"F4.wireOp",EDGE,"E83.MirrorCS"),sQuery(id+"F4.wireOp",EDGE,"E94.MirrorCS")])]});
            var Q39;
            Q39=makeQuery(id+"F5.opExtrude","SWEPT_BODY",BODY,{"disambiguationData":[OSD([sQuery(id+"F4.wireOp",EDGE,"E79.MirrorCS"),sQuery(id+"F4.wireOp",EDGE,"E86.MirrorCS"),sQuery(id+"F4.wireOp",EDGE,"E89.MirrorCS"),sQuery(id+"F4.wireOp",EDGE,"E94.MirrorCS")])]});
            var Q40;
            Q40=makeQuery(id+"F5.opExtrude","SWEPT_BODY",BODY,{"disambiguationData":[OSD([sQuery(id+"F4.wireOp",EDGE,"E62.MirrorCS"),sQuery(id+"F4.wireOp",EDGE,"E63.MirrorCS"),sQuery(id+"F4.wireOp",EDGE,"E66.top"),sQuery(id+"F4.wireOp",EDGE,"E68.bottom")])]});
            var Q41;
            Q41=makeQuery(id+"F5.opExtrude","SWEPT_BODY",BODY,{"disambiguationData":[OSD([sQuery(id+"F4.wireOp",EDGE,"E84.MirrorCS"),sQuery(id+"F4.wireOp",EDGE,"E86.MirrorCS"),sQuery(id+"F4.wireOp",EDGE,"E89.MirrorCS"),sQuery(id+"F4.wireOp",EDGE,"E103.MirrorCS")])]});
            var Q42;
            Q42=makeQuery(id+"F5.opExtrude","SWEPT_BODY",BODY,{"disambiguationData":[OSD([sQuery(id+"F4.wireOp",EDGE,"E84.MirrorCS"),sQuery(id+"F4.wireOp",EDGE,"E90.MirrorCS"),sQuery(id+"F4.wireOp",EDGE,"E91.MirrorCS"),sQuery(id+"F4.wireOp",EDGE,"E103.MirrorCS")])]});
            var Q43;
            Q43=makeQuery(id+"F2.opExtrude","SWEPT_BODY",BODY,{"disambiguationData":[OSD([sQuery(id+"F0.wireOp",EDGE,"E41.MirrorCS"),sQuery(id+"F0.wireOp",EDGE,"E50.MirrorCS"),sQuery(id+"F0.wireOp",EDGE,"E53.MirrorCS"),sQuery(id+"F0.wireOp",EDGE,"E54.MirrorCS")])]});
            var Q44;
            Q44=makeQuery(id+"F2.opExtrude","SWEPT_BODY",BODY,{"disambiguationData":[OSD([sQuery(id+"F0.wireOp",EDGE,"E10.left"),sQuery(id+"F0.wireOp",EDGE,"E10.right"),sQuery(id+"F0.wireOp",EDGE,"E17.top"),sQuery(id+"F0.wireOp",EDGE,"E19.bottom")])]});
            var Q45;
            Q45=makeQuery(id+"F2.opExtrude","SWEPT_BODY",BODY,{"disambiguationData":[OSD([sQuery(id+"F0.wireOp",EDGE,"E10.left"),sQuery(id+"F0.wireOp",EDGE,"E10.right"),sQuery(id+"F0.wireOp",EDGE,"E19.top"),sQuery(id+"F0.wireOp",EDGE,"E21.bottom")])]});
            var Q46;
            Q46=makeQuery(id+"F5.opExtrude","SWEPT_BODY",BODY,{"disambiguationData":[OSD([sQuery(id+"F4.wireOp",EDGE,"E60.left"),sQuery(id+"F4.wireOp",EDGE,"E60.right"),sQuery(id+"F4.wireOp",EDGE,"E66.top"),sQuery(id+"F4.wireOp",EDGE,"E68.bottom")])]});
            var Q47;
            Q47=makeQuery(id+"F5.opExtrude","SWEPT_BODY",BODY,{"disambiguationData":[OSD([sQuery(id+"F4.wireOp",EDGE,"E60.left"),sQuery(id+"F4.wireOp",EDGE,"E60.right"),sQuery(id+"F4.wireOp",EDGE,"E68.top"),sQuery(id+"F4.wireOp",EDGE,"E70.bottom")])]});
            var Q48;
            Q48=makeQuery(id+"F2.opExtrude","SWEPT_BODY",BODY,{"disambiguationData":[OSD([sQuery(id+"F0.wireOp",EDGE,"E29.MirrorCS"),sQuery(id+"F0.wireOp",EDGE,"E49.MirrorCS"),sQuery(id+"F0.wireOp",EDGE,"E50.MirrorCS"),sQuery(id+"F0.wireOp",EDGE,"E54.MirrorCS")])]});
            booleanBodies(context, id + "F7", {"operationType" : BooleanOperationType.UNION, "tools" : qUnion([Q0, Q1, Q2, Q3, Q4, Q5, Q6, Q7, Q8, Q9, Q10, Q11, Q12, Q13, Q14, Q15, Q16, Q17, Q18, Q19, Q20, Q21, Q22, Q23, Q24, Q25, Q26, Q27, Q28, Q29, Q30, Q31, Q32, Q33, Q34, Q35, Q36, Q37, Q38, Q39, Q40, Q41, Q42, Q43, Q44, Q45, Q46, Q47, Q48])});
        }
    });
